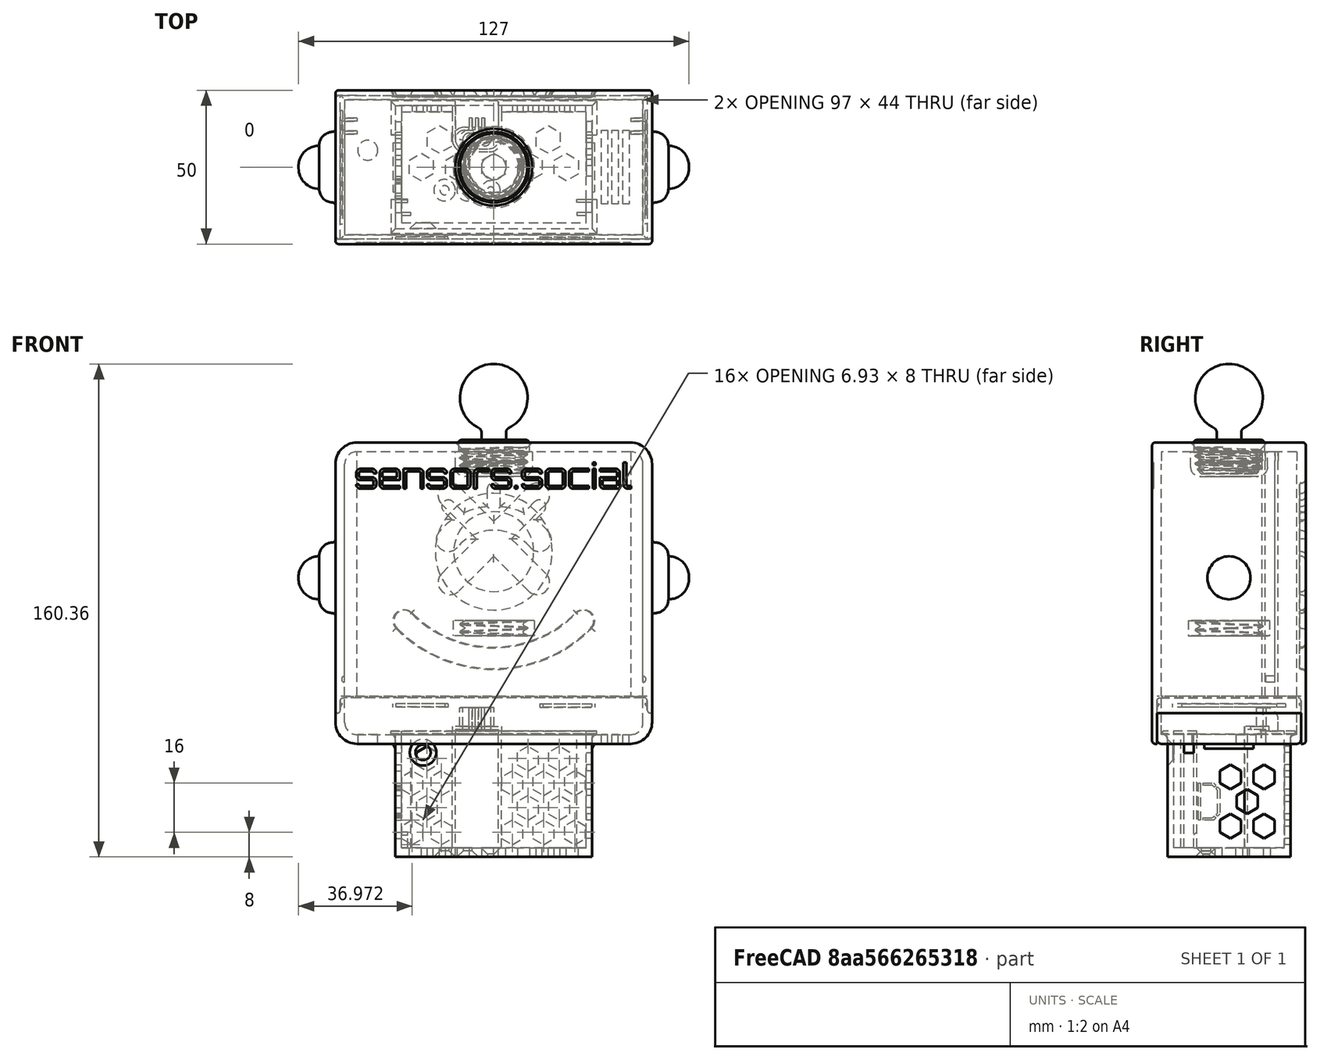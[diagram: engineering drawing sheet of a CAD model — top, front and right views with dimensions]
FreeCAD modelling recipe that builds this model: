
FCSTD DOCUMENT  (FreeCAD 1.1RUnknown)
Label: Altruist_Urban
License: All rights reserved
LicenseURL: http://en.wikipedia.org/wiki/All_rights_reserved
objects: Sketcher::SketchObject×33, PartDesign::Fillet×20, PartDesign::Pad×19, PartDesign::Pocket×16, App::Point×8, PartDesign::Body×8, PartDesign::Mirrored×5, PartDesign::Chamfer×5, PartDesign::FeatureBase×4, PartDesign::Thickness×2, PartDesign::Revolution×1, PartDesign::LinearPattern×1, PartDesign::Groove×1, Part::Part2DObjectPython×1, Part::FeaturePython×1, PartDesign::Boolean×1, PartDesign::Hole×1
note: 293 computed .brp shape members not serialized (recipe doc carries the construction recipe); baked Part::Feature solids carry a one-line shape summary decoded from their .brp

FEATURE [Sketcher::SketchObject] Sketch
  ArcFitTolerance = 1e-06
  AttachmentSupport = -> [XZ_Plane]
  ExternalTypes = [0]
  FullyConstrained = true
  MakeInternals = false
  MapMode = 5
  Placement = pos=(0,0,0) rot=(1,0,0;1.5708rad)
  _ExternalGeoVersion = 0
  sketch-geometry (4):
    g0: LineSegment StartX=-51.5 StartY=44 StartZ=0 EndX=-51.5 EndY=-44 EndZ=0
    g1: LineSegment StartX=-51.5 StartY=-44 StartZ=0 EndX=51.5 EndY=-44 EndZ=0
    g2: LineSegment StartX=51.5 StartY=-44 StartZ=0 EndX=51.5 EndY=44 EndZ=0
    g3: LineSegment StartX=51.5 StartY=44 StartZ=0 EndX=-51.5 EndY=44 EndZ=0
  constraints (11):
    c: Coincident(g0,g1)
    c: Coincident(g1,g2)
    c: Coincident(g2,g3)
    c: Coincident(g3,g0)
    c: Vertical(g0)
    c: Vertical(g2)
    c: Horizontal(g1)
    c: Horizontal(g3)
    c: DistanceX(g3,g3) = 103
    c: DistanceY(g2,g2) = 88
    c: Symmetric(g2,g0,g-1)
FEATURE [PartDesign::Pad] Pad
  Direction = (0,-1,2e-16)
  Length = 25
  Length2 = 25
  Placement = pos=(0,0,0) rot=(1,0,0;1.5708rad)
  Profile = -> Sketch
  ReferenceAxis = -> Sketch [N_Axis]
  Reversed = true
  SideType = 1
  Suppressed = false
  Type = 0
  Type2 = 0
FEATURE [PartDesign::Fillet] Fillet
  Base = -> Pad [Edge1,Edge8]
  BaseFeature = -> Pad
  Placement = pos=(0,0,0) rot=(1,0,0;1.5708rad)
  Radius = 7
  SupportTransform = false
  Suppressed = false
  UseAllEdges = false
FEATURE [Sketcher::SketchObject] Sketch009
  ArcFitTolerance = 1e-06
  AttachmentSupport = -> [XZ_Plane001]
  ExternalTypes = [0]
  FullyConstrained = true
  MakeInternals = false
  MapMode = 5
  Placement = pos=(0,0,0) rot=(1,0,0;1.5708rad)
  _ExternalGeoVersion = 0
  sketch-geometry (14):
    g0: ArcOfCircle CenterX=0 CenterY=6.86 CenterZ=0 NormalX=0 NormalY=0 NormalZ=1 AngleXU=0 Radius=11 StartAngle=5.16799 EndAngle=7.85398
    g1: LineSegment StartX=4 StartY=-6.86497 StartZ=0 EndX=10.5 EndY=-6.86497 EndZ=0
    g2: ArcOfCircle CenterX=10.5 CenterY=-7.86497 CenterZ=0 NormalX=0 NormalY=0 NormalZ=1 AngleXU=0 Radius=1 StartAngle=0 EndAngle=1.5708
    g3: LineSegment StartX=0 StartY=17.86 StartZ=0 EndX=0 EndY=-17.86 EndZ=0
    g4: LineSegment StartX=4 StartY=-6.86497 StartZ=0 EndX=4 EndY=-4.36497 EndZ=0
    g5: ArcOfCircle CenterX=5.5 CenterY=-4.36497 CenterZ=0 NormalX=0 NormalY=0 NormalZ=1 AngleXU=0 Radius=1.5 StartAngle=2.0264 EndAngle=3.14159
    g6: LineSegment [constr] StartX=0 StartY=6.86 StartZ=0 EndX=5.5 EndY=-4.36497 EndZ=0
    g7: LineSegment StartX=0 StartY=-17.86 StartZ=0 EndX=9 EndY=-17.86 EndZ=0
    g8: LineSegment StartX=9 StartY=-17.86 StartZ=0 EndX=10.7 EndY=-16.16 EndZ=0
    g9: LineSegment StartX=11.5 StartY=-7.86497 StartZ=0 EndX=11.5 EndY=-13.81 EndZ=0
    g10: LineSegment StartX=11.5 StartY=-13.81 StartZ=0 EndX=8.2 EndY=-13.81 EndZ=0
    g11: LineSegment StartX=8.2 StartY=-13.81 StartZ=0 EndX=8.2 EndY=-14.31 EndZ=0
    g12: LineSegment StartX=8.2 StartY=-14.31 StartZ=0 EndX=10.7 EndY=-14.31 EndZ=0
    g13: LineSegment StartX=10.7 StartY=-14.31 StartZ=0 EndX=10.7 EndY=-16.16 EndZ=0
  constraints (42):
    c: PointOnObject(g0,g-2)
    c: Radius(g0) = 11
    c: Horizontal(g1)
    c: Coincident(g2,g1)
    c: Coincident(g3,g0)
    c: Vertical(g1,g2)
    c: Horizontal(g2,g2)
    c: Radius(g2) = 1
    c: PointOnObject(g0,g3)
    c: Symmetric(g3,g0,g-1)
    c: Coincident(g4,g1)
    c: Vertical(g4)
    c: Coincident(g5,g0)
    c: Coincident(g5,g4)
    c: Horizontal(g4,g5)
    c: Coincident(g6,g0)
    c: Coincident(g6,g5)
    c: PointOnObject(g0,g6)
    c: Radius(g5) = 1.5
    c: DistanceY(g4,g4) = 2.5
    c: Distance(g3,g4) = 4
    c: DistanceY(g3,g3) = 35.72
    c: DistanceX(g1,g1) = 6.5
    c: Coincident(g3,g7)
    c: Horizontal(g7)
    c: Coincident(g7,g8)
    c: Angle(g8,g7) = 2.35619
    c: DistanceX(g7,g7) = 9
    c: Tangent(g2,g9) = 1.5708
    c: Coincident(g9,g10)
    c: Coincident(g10,g11)
    c: Vertical(g11)
    c: Coincident(g11,g12)
    c: Horizontal(g12)
    c: Coincident(g12,g13)
    c: Coincident(g13,g8)
    c: Vertical(g13)
    c: DistanceY(g11,g11) = 0.5
    c: Distance(g13,g3) = 10.7
    c: Distance(g12,g12) = 2.5
    c: DistanceY(g13,g13) = 1.85
    c: Horizontal(g10)
FEATURE [PartDesign::Revolution] Revolution
  Angle = 360
  Angle2 = 60
  Axis = (0,2e-16,1)
  Base = (0,0,0)
  FuseOrder = 1
  Placement = pos=(0,0,0) rot=(1,0,0;1.5708rad)
  Profile = -> Sketch009
  ReferenceAxis = -> Sketch009 [V_Axis]
  Reversed = true
  Suppressed = false
  Type = 0
FEATURE [Sketcher::SketchObject] Sketch010
  ArcFitTolerance = 1e-06
  AttachmentSupport = -> [XZ_Plane002]
  ExternalTypes = [0]
  FullyConstrained = true
  MakeInternals = false
  MapMode = 5
  Placement = pos=(0,0,0) rot=(1,0,0;1.5708rad)
  _ExternalGeoVersion = 0
  sketch-geometry (4):
    g0: LineSegment StartX=-51.5 StartY=7.5 StartZ=0 EndX=-51.5 EndY=-7.5 EndZ=0
    g1: LineSegment StartX=-51.5 StartY=-7.5 StartZ=0 EndX=51.5 EndY=-7.5 EndZ=0
    g2: LineSegment StartX=51.5 StartY=-7.5 StartZ=0 EndX=51.5 EndY=7.5 EndZ=0
    g3: LineSegment StartX=51.5 StartY=7.5 StartZ=0 EndX=-51.5 EndY=7.5 EndZ=0
  constraints (11):
    c: Coincident(g0,g1)
    c: Coincident(g1,g2)
    c: Coincident(g2,g3)
    c: Coincident(g3,g0)
    c: Vertical(g0)
    c: Vertical(g2)
    c: Horizontal(g1)
    c: Horizontal(g3)
    c: DistanceX(g3,g3) = 103
    c: Symmetric(g2,g0,g-1)
    c: DistanceY(g2,g2) = 15
FEATURE [PartDesign::Pad] Pad005
  Direction = (0,-1,2e-16)
  Length = 25
  Length2 = 25
  Placement = pos=(0,0,0) rot=(1,0,0;1.5708rad)
  Profile = -> Sketch010
  ReferenceAxis = -> Sketch010 [N_Axis]
  Reversed = true
  SideType = 1
  Suppressed = false
  Type = 0
  Type2 = 0
FEATURE [PartDesign::Fillet] Fillet004
  Base = -> Pad005 [Edge2,Edge5]
  BaseFeature = -> Pad005
  Placement = pos=(0,0,0) rot=(1,0,0;1.5708rad)
  Radius = 7
  SupportTransform = false
  Suppressed = false
  UseAllEdges = false
FEATURE [PartDesign::Thickness] Thickness001
  Base = -> Fillet004 [Face4]
  BaseFeature = -> Fillet004
  Intersection = false
  Join = 0
  Mode = 0
  Reversed = true
  SupportTransform = false
  Suppressed = false
  Value = 3
FEATURE [Sketcher::SketchObject] Sketch011
  ArcFitTolerance = 1e-06
  AttachmentSupport = -> [Thickness001]
  ExternalTypes = [0]
  FullyConstrained = true
  MakeInternals = false
  MapMode = 5
  Placement = pos=(0,-1e-15,-4.5) rot=(0,0,1;0rad)
  _ExternalGeoVersion = 0
  sketch-geometry (4):
    g0: LineSegment StartX=-32 StartY=20 StartZ=0 EndX=-32 EndY=-20 EndZ=0
    g1: LineSegment StartX=-32 StartY=-20 StartZ=0 EndX=32 EndY=-20 EndZ=0
    g2: LineSegment StartX=32 StartY=-20 StartZ=0 EndX=32 EndY=20 EndZ=0
    g3: LineSegment StartX=32 StartY=20 StartZ=0 EndX=-32 EndY=20 EndZ=0
  constraints (11):
    c: Coincident(g0,g1)
    c: Coincident(g1,g2)
    c: Coincident(g2,g3)
    c: Coincident(g3,g0)
    c: Vertical(g0)
    c: Vertical(g2)
    c: Horizontal(g1)
    c: Horizontal(g3)
    c: Symmetric(g2,g0,g-1)
    c: DistanceY(g2,g2) = 40
    c: DistanceX(g3,g3) = 64
FEATURE [PartDesign::Pocket] Pocket002
  BaseFeature = -> Thickness001
  Direction = (0,0,-1)
  Length = 5
  Length2 = 5
  Profile = -> Sketch011
  ReferenceAxis = -> Sketch011 [N_Axis]
  SideType = 0
  Suppressed = false
  Type = 1
  Type2 = 0
FEATURE [Sketcher::SketchObject] Sketch012
  ArcFitTolerance = 1e-06
  AttachmentSupport = -> [Pocket002]
  ExternalTypes = [0]
  FullyConstrained = true
  MakeInternals = false
  MapMode = 5
  Placement = pos=(0,1.7e-15,7.5) rot=(0,0,1;0rad)
  _ExternalGeoVersion = 0
  sketch-geometry (8):
    g0: LineSegment StartX=-49.9 StartY=23.4 StartZ=0 EndX=-49.9 EndY=-23.4 EndZ=0
    g1: LineSegment StartX=-49.9 StartY=-23.4 StartZ=0 EndX=49.9 EndY=-23.4 EndZ=0
    g2: LineSegment StartX=49.9 StartY=-23.4 StartZ=0 EndX=49.9 EndY=23.4 EndZ=0
    g3: LineSegment StartX=49.9 StartY=23.4 StartZ=0 EndX=-49.9 EndY=23.4 EndZ=0
    g4: LineSegment StartX=-51.5 StartY=25 StartZ=0 EndX=-51.5 EndY=-25 EndZ=0
    g5: LineSegment StartX=-51.5 StartY=-25 StartZ=0 EndX=51.5 EndY=-25 EndZ=0
    g6: LineSegment StartX=51.5 StartY=-25 StartZ=0 EndX=51.5 EndY=25 EndZ=0
    g7: LineSegment StartX=51.5 StartY=25 StartZ=0 EndX=-51.5 EndY=25 EndZ=0
  constraints (22):
    c: Coincident(g0,g1)
    c: Coincident(g1,g2)
    c: Coincident(g2,g3)
    c: Coincident(g3,g0)
    c: Vertical(g0)
    c: Vertical(g2)
    c: Horizontal(g1)
    c: Horizontal(g3)
    c: Symmetric(g0,g2,g-1)
    c: DistanceX(g3,g3) = 99.8
    c: DistanceY(g2,g2) = 46.8
    c: Coincident(g4,g5)
    c: Coincident(g5,g6)
    c: Coincident(g6,g7)
    c: Coincident(g7,g4)
    c: Vertical(g4)
    c: Vertical(g6)
    c: Horizontal(g5)
    c: Horizontal(g7)
    c: Symmetric(g4,g6,g-1)
    c: DistanceY(g6,g6) = 50
    c: DistanceX(g7,g7) = 103
FEATURE [PartDesign::Pocket] Pocket003
  BaseFeature = -> Pocket002
  Direction = (0,0,-1)
  Length = 5
  Length2 = 5
  Profile = -> Sketch012
  ReferenceAxis = -> Sketch012 [N_Axis]
  SideType = 0
  Suppressed = false
  Type = 0
  Type2 = 0
FEATURE [Sketcher::SketchObject] Sketch013
  ArcFitTolerance = 1e-06
  AttachmentSupport = -> [Pocket003]
  ExternalTypes = [0]
  FullyConstrained = true
  MakeInternals = false
  MapMode = 5
  Placement = pos=(0,-23.4,0) rot=(1,0,0;1.5708rad)
  _ExternalGeoVersion = 0
  sketch-geometry (6):
    g0: LineSegment StartX=49.9 StartY=5.55 StartZ=0 EndX=49.9 EndY=4.45 EndZ=0
    g1: LineSegment StartX=-49.15 StartY=5.55 StartZ=0 EndX=-49.9 EndY=5.55 EndZ=0
    g2: LineSegment StartX=-49.9 StartY=5.55 StartZ=0 EndX=-49.9 EndY=4.45 EndZ=0
    g3: LineSegment StartX=-49.9 StartY=4.45 StartZ=0 EndX=-49.15 EndY=5.55 EndZ=0
    g4: LineSegment StartX=49.9 StartY=5.55 StartZ=0 EndX=49.15 EndY=5.55 EndZ=0
    g5: LineSegment StartX=49.15 StartY=5.55 StartZ=0 EndX=49.9 EndY=4.45 EndZ=0
  constraints (17):
    c: Vertical(g0)
    c: Coincident(g1,g2)
    c: Vertical(g2)
    c: Equal(g0,g2)
    c: DistanceY(g0,g0) = 1.1
    c: Symmetric(g0,g2,g-2)
    c: DistanceX(g1,g0) = 99.8
    c: Coincident(g3,g2)
    c: Coincident(g3,g1)
    c: Coincident(g0,g4)
    c: Horizontal(g4)
    c: Coincident(g4,g5)
    c: Coincident(g5,g0)
    c: DistanceX(g4,g4) = 0.75
    c: Distance(g0,g-1) = 4.45
    c: Horizontal(g1)
    c: Equal(g1,g4)
FEATURE [PartDesign::Thickness] Thickness
  Base = -> Fillet [Face4]
  BaseFeature = -> Fillet
  Intersection = false
  Join = 0
  Mode = 0
  Reversed = true
  SupportTransform = false
  Suppressed = false
  Value = 3
FEATURE [Sketcher::SketchObject] Sketch004
  ArcFitTolerance = 1e-06
  AttachmentSupport = -> [Thickness]
  ExternalTypes = [0]
  FullyConstrained = true
  MakeInternals = false
  MapMode = 5
  Placement = pos=(0,-1.94e-14,-44) rot=(1,0,0;3.14159rad)
  _ExternalGeoVersion = 0
  sketch-geometry (4):
    g0: LineSegment StartX=-49.9 StartY=23.4 StartZ=0 EndX=-49.9 EndY=-23.4 EndZ=0
    g1: LineSegment StartX=-49.9 StartY=-23.4 StartZ=0 EndX=49.9 EndY=-23.4 EndZ=0
    g2: LineSegment StartX=49.9 StartY=-23.4 StartZ=0 EndX=49.9 EndY=23.4 EndZ=0
    g3: LineSegment StartX=49.9 StartY=23.4 StartZ=0 EndX=-49.9 EndY=23.4 EndZ=0
  constraints (11):
    c: Coincident(g0,g1)
    c: Coincident(g1,g2)
    c: Coincident(g2,g3)
    c: Coincident(g3,g0)
    c: Vertical(g0)
    c: Vertical(g2)
    c: Horizontal(g1)
    c: Horizontal(g3)
    c: Symmetric(g0,g2,g-1)
    c: DistanceX(g3,g3) = 99.8
    c: DistanceY(g2,g2) = 46.8
FEATURE [PartDesign::Pocket] Pocket001
  BaseFeature = -> Thickness
  Direction = (0,0,1)
  Length = 5.5
  Length2 = 5
  Profile = -> Sketch004
  ReferenceAxis = -> Sketch004 [N_Axis]
  SideType = 0
  Suppressed = false
  Type = 0
  Type2 = 0
FEATURE [Sketcher::SketchObject] Sketch005
  ArcFitTolerance = 1e-06
  AttachmentSupport = -> [Pocket001]
  ExternalGeometry = -> [Pocket001]
  ExternalTypes = [0]
  FullyConstrained = true
  MakeInternals = false
  MapMode = 5
  Placement = pos=(0,22,0) rot=(1,0,0;1.5708rad)
  _ExternalGeoVersion = 0
  sketch-geometry (8):
    g0: LineSegment StartX=-48.5 StartY=-38.5 StartZ=0 EndX=-48.5 EndY=37 EndZ=0
    g1: LineSegment StartX=-48.5 StartY=-38.5 StartZ=0 EndX=-44.5 EndY=-38.5 EndZ=0
    g2: LineSegment StartX=-44.5 StartY=-38.5 StartZ=0 EndX=-44.5 EndY=41 EndZ=0
    g3: LineSegment StartX=44.5 StartY=41 StartZ=0 EndX=44.5 EndY=-38.5 EndZ=0
    g4: LineSegment StartX=44.5 StartY=-38.5 StartZ=0 EndX=48.5 EndY=-38.5 EndZ=0
    g5: LineSegment StartX=48.5 StartY=-38.5 StartZ=0 EndX=48.5 EndY=37 EndZ=0
    g6: ArcOfCircle CenterX=44.5 CenterY=37 CenterZ=0 NormalX=0 NormalY=0 NormalZ=1 AngleXU=0 Radius=4 StartAngle=0 EndAngle=1.5708
    g7: ArcOfCircle CenterX=-44.5 CenterY=37 CenterZ=0 NormalX=0 NormalY=0 NormalZ=1 AngleXU=0 Radius=4 StartAngle=1.5708 EndAngle=3.14159
  constraints (22):
    c: Coincident(g0,g-4)
    c: Coincident(g1,g0)
    c: Horizontal(g1)
    c: Coincident(g2,g1)
    c: Vertical(g2)
    c: Vertical(g3)
    c: Coincident(g4,g3)
    c: Coincident(g5,g4)
    c: Coincident(g6,g3)
    c: Coincident(g7,g2)
    c: Coincident(g7,g0)
    c: PointOnObject(g7,g2)
    c: Coincident(g2,g-3)
    c: Coincident(g0,g-4)
    c: Coincident(g5,g6)
    c: Symmetric(g3,g1,g-2)
    c: Vertical(g5)
    c: Equal(g4,g1)
    c: PointOnObject(g6,g3)
    c: Horizontal(g6,g5)
    c: Horizontal(g4)
    c: Horizontal(g3,g2)
FEATURE [PartDesign::Pad] Pad004
  BaseFeature = -> Pocket001
  Direction = (0,-1,2e-16)
  Length = -6
  Length2 = 7
  Profile = -> Sketch005
  ReferenceAxis = -> Sketch005 [N_Axis]
  Reversed = true
  SideType = 1
  Suppressed = false
  Type = 0
  Type2 = 0
FEATURE [PartDesign::LinearPattern] LinearPattern
  BaseFeature = -> Pad004
  Direction = -> Y_Axis
  Length = 4.2
  Length2 = 100
  Mode = 0
  Mode2 = 0
  Occurrences = 2
  Occurrences2 = 1
  Offset = 4.2
  Offset2 = 10
  Originals = -> [Pad004]
  Reversed = true
  Reversed2 = false
  SpacingPattern = [0]
  SpacingPattern2 = [0]
  Spacings = [-1]
  Suppressed = false
  TransformMode = 0
FEATURE [Sketcher::SketchObject] Sketch006
  ArcFitTolerance = 1e-06
  AttachmentSupport = -> [LinearPattern]
  ExternalGeometry = -> [LinearPattern]
  ExternalTypes = [0]
  FullyConstrained = true
  MakeInternals = false
  MapMode = 5
  Placement = pos=(48.5,0,0) rot=(0.57735,-0.57735,-0.57735;2.0944rad)
  _ExternalGeoVersion = 0
  sketch-geometry (4):
    g0: LineSegment StartX=-12 StartY=-33 StartZ=0 EndX=-15 EndY=-33 EndZ=0
    g1: LineSegment StartX=-15 StartY=-33 StartZ=0 EndX=-15 EndY=-34 EndZ=0
    g2: LineSegment StartX=-15 StartY=-34 StartZ=0 EndX=-12 EndY=-34 EndZ=0
    g3: LineSegment StartX=-12 StartY=-34 StartZ=0 EndX=-12 EndY=-33 EndZ=0
  constraints (12):
    c: Coincident(g0,g1)
    c: Coincident(g1,g2)
    c: Coincident(g2,g3)
    c: Coincident(g3,g0)
    c: Horizontal(g0)
    c: Horizontal(g2)
    c: Vertical(g1)
    c: Vertical(g3)
    c: PointOnObject(g0,g-4)
    c: PointOnObject(g1,g-3)
    c: Distance(g-5,g2) = 5
    c: DistanceY(g3,g3) = 1
FEATURE [PartDesign::Groove] Groove
  Angle = 180
  Angle2 = 60
  Axis = (0,1,0)
  Base = (48.5,12,-33)
  BaseFeature = -> LinearPattern
  Profile = -> Sketch006
  ReferenceAxis = -> Sketch006 [Edge1]
  Reversed = true
  Suppressed = false
  Type = 0
FEATURE [PartDesign::Mirrored] Mirrored001
  BaseFeature = -> Groove
  MirrorPlane = -> YZ_Plane
  Originals = -> [Groove]
  Suppressed = false
  TransformMode = 0
FEATURE [Sketcher::SketchObject] Sketch007
  ArcFitTolerance = 1e-06
  AttachmentSupport = -> [Mirrored001]
  ExternalTypes = [0]
  FullyConstrained = true
  MakeInternals = false
  MapMode = 5
  Placement = pos=(-49.9,0,0) rot=(0.57735,0.57735,0.57735;2.0944rad)
  _ExternalGeoVersion = 0
  sketch-geometry (6):
    g0: LineSegment StartX=-23.4 StartY=-41 StartZ=0 EndX=-23.4 EndY=-42 EndZ=0
    g1: LineSegment StartX=23.4 StartY=-41 StartZ=0 EndX=23.4 EndY=-42 EndZ=0
    g2: LineSegment StartX=-23.4 StartY=-41 StartZ=0 EndX=-22.8 EndY=-41 EndZ=0
    g3: LineSegment StartX=-22.8 StartY=-41 StartZ=0 EndX=-23.4 EndY=-42 EndZ=0
    g4: LineSegment StartX=23.4 StartY=-41 StartZ=0 EndX=22.8 EndY=-41 EndZ=0
    g5: LineSegment StartX=22.8 StartY=-41 StartZ=0 EndX=23.4 EndY=-42 EndZ=0
  constraints (17):
    c: Vertical(g0)
    c: Vertical(g1)
    c: Equal(g0,g1)
    c: DistanceY(g1,g1) = 1
    c: Symmetric(g0,g1,g-2)
    c: Distance(g0,g1) = 46.8
    c: Coincident(g0,g2)
    c: Horizontal(g2)
    c: Coincident(g2,g3)
    c: Coincident(g3,g0)
    c: Coincident(g1,g4)
    c: Horizontal(g4)
    c: Coincident(g4,g5)
    c: Coincident(g5,g1)
    c: Equal(g4,g2)
    c: DistanceY(g1,g-1) = 41
    c: DistanceX(g4,g4) = 0.6
FEATURE [Sketcher::SketchObject] Sketch008
  ArcFitTolerance = 1e-06
  AttachmentSupport = -> [Pocket001]
  ExternalTypes = [0]
  FullyConstrained = true
  MakeInternals = false
  MapMode = 5
  Placement = pos=(0,23.4,0) rot=(1,0,0;1.5708rad)
  _ExternalGeoVersion = 0
  sketch-geometry (6):
    g0: LineSegment StartX=-49.9 StartY=-41 StartZ=0 EndX=-49.9 EndY=-42 EndZ=0
    g1: LineSegment StartX=49.9 StartY=-41 StartZ=0 EndX=49.9 EndY=-42 EndZ=0
    g2: LineSegment StartX=49.9 StartY=-41 StartZ=0 EndX=49.3 EndY=-41 EndZ=0
    g3: LineSegment StartX=49.3 StartY=-41 StartZ=0 EndX=49.9 EndY=-42 EndZ=0
    g4: LineSegment StartX=-49.9 StartY=-41 StartZ=0 EndX=-49.3 EndY=-41 EndZ=0
    g5: LineSegment StartX=-49.3 StartY=-41 StartZ=0 EndX=-49.9 EndY=-42 EndZ=0
  constraints (17):
    c: Vertical(g0)
    c: Vertical(g1)
    c: Equal(g0,g1)
    c: DistanceY(g1,g1) = 1
    c: Symmetric(g0,g1,g-2)
    c: Distance(g0,g1) = 99.8
    c: Coincident(g1,g2)
    c: Horizontal(g2)
    c: Coincident(g2,g3)
    c: Coincident(g3,g1)
    c: DistanceX(g2,g2) = 0.6
    c: Distance(g-1,g2) = 41
    c: Coincident(g0,g4)
    c: Horizontal(g4)
    c: Coincident(g4,g5)
    c: Coincident(g5,g0)
    c: Equal(g4,g2)
FEATURE [PartDesign::Fillet] Fillet023
  Base = -> Mirrored001 [Edge17,Edge15]
  BaseFeature = -> Mirrored001
  Radius = 1
  Refine = true
  SupportTransform = false
  Suppressed = false
  UseAllEdges = false
FEATURE [App::Point] Origin017  label="Origin"
  Role = Origin
FEATURE [App::Point] Origin018  label="Origin"
  Role = Origin
FEATURE [App::Point] Origin024  label="Origin"
  Role = Origin
FEATURE [App::Point] Origin025  label="Origin"
  Role = Origin
FEATURE [App::Point] Origin026  label="Origin"
  Role = Origin
FEATURE [App::Point] Origin029  label="Origin"
  Role = Origin
FEATURE [App::Point] Origin030  label="Origin"
  Role = Origin
FEATURE [App::Point] Origin032
  Role = Origin
FEATURE [Sketcher::SketchObject] Sketch099
  ArcFitTolerance = 1e-06
  AttachmentSupport = -> [XY_Plane017]
  ExternalTypes = [0]
  FullyConstrained = true
  MakeInternals = false
  MapMode = 5
  _ExternalGeoVersion = 0
  sketch-geometry (32):
    g0: LineSegment StartX=-32 StartY=-20 StartZ=0 EndX=32 EndY=-20 EndZ=0
    g1: LineSegment StartX=-32 StartY=20 StartZ=0 EndX=-32 EndY=-20 EndZ=0
    g2: LineSegment StartX=32 StartY=20 StartZ=0 EndX=32 EndY=-20 EndZ=0
    g3: LineSegment StartX=-30 StartY=-18 StartZ=0 EndX=30 EndY=-18 EndZ=0
    g4: LineSegment StartX=-30 StartY=18 StartZ=0 EndX=-13.5 EndY=18 EndZ=0
    g5: LineSegment StartX=30 StartY=18 StartZ=0 EndX=2.5 EndY=18 EndZ=0
    g6: LineSegment StartX=-9.5 StartY=5 StartZ=0 EndX=-1.5 EndY=5 EndZ=0
    g7: LineSegment StartX=-32 StartY=20 StartZ=0 EndX=-12.5 EndY=20 EndZ=0
    g8: LineSegment StartX=32 StartY=20 StartZ=0 EndX=1.5 EndY=20 EndZ=0
    g9: LineSegment StartX=-9.5 StartY=6 StartZ=0 EndX=-1.5 EndY=6 EndZ=0
    g10: LineSegment StartX=-12.5 StartY=20 StartZ=0 EndX=-12.5 EndY=9 EndZ=0
    g11: LineSegment StartX=1.5 StartY=20 StartZ=0 EndX=1.5 EndY=9 EndZ=0
    g12: ArcOfCircle CenterX=-9.5 CenterY=9 CenterZ=0 NormalX=0 NormalY=0 NormalZ=1 AngleXU=0 Radius=3 StartAngle=3.14159 EndAngle=4.71239
    g13: ArcOfCircle CenterX=-1.5 CenterY=9 CenterZ=0 NormalX=0 NormalY=0 NormalZ=1 AngleXU=0 Radius=3 StartAngle=4.71239 EndAngle=6.28319
    g14: LineSegment StartX=-13.5 StartY=18 StartZ=0 EndX=-13.5 EndY=9 EndZ=0
    g15: LineSegment StartX=2.5 StartY=18 StartZ=0 EndX=2.5 EndY=9 EndZ=0
    g16: ArcOfCircle CenterX=-9.5 CenterY=9 CenterZ=0 NormalX=0 NormalY=0 NormalZ=1 AngleXU=0 Radius=4 StartAngle=3.14159 EndAngle=4.71239
    g17: ArcOfCircle CenterX=-1.5 CenterY=9 CenterZ=0 NormalX=0 NormalY=0 NormalZ=1 AngleXU=0 Radius=4 StartAngle=4.71239 EndAngle=6.28319
    g18: LineSegment StartX=-30 StartY=-15.7 StartZ=0 EndX=-27 EndY=-15.7 EndZ=0
    g19: LineSegment StartX=-27 StartY=-15.7 StartZ=0 EndX=-27 EndY=-14.7 EndZ=0
    g20: LineSegment StartX=-27 StartY=-14.7 StartZ=0 EndX=-30 EndY=-14.7 EndZ=0
    g21: LineSegment StartX=30 StartY=-14.7 StartZ=0 EndX=27 EndY=-14.7 EndZ=0
    g22: LineSegment StartX=27 StartY=-14.7 StartZ=0 EndX=27 EndY=-15.7 EndZ=0
    g23: LineSegment StartX=27 StartY=-15.7 StartZ=0 EndX=30 EndY=-15.7 EndZ=0
    g24: LineSegment StartX=-30 StartY=18 StartZ=0 EndX=-30 EndY=-14.7 EndZ=0
    g25: LineSegment StartX=-30 StartY=-15.7 StartZ=0 EndX=-30 EndY=-18 EndZ=0
    g26: LineSegment StartX=30 StartY=-18 StartZ=0 EndX=30 EndY=-15.7 EndZ=0
    g27: LineSegment StartX=30 StartY=-14.7 StartZ=0 EndX=30 EndY=-11.5 EndZ=0
    g28: LineSegment StartX=30 StartY=-11.5 StartZ=0 EndX=27 EndY=-11.5 EndZ=0
    g29: LineSegment StartX=27 StartY=-11.5 StartZ=0 EndX=27 EndY=-10.5 EndZ=0
    g30: LineSegment StartX=27 StartY=-10.5 StartZ=0 EndX=30 EndY=-10.5 EndZ=0
    g31: LineSegment StartX=30 StartY=-10.5 StartZ=0 EndX=30 EndY=18 EndZ=0
  constraints (95):
    c: Horizontal(g0)
    c: Symmetric(g2,g0,g-1)
    c: DistanceY(g0,g2) = 40
    c: DistanceX(g1,g2) = 64
    c: Vertical(g1)
    c: Vertical(g2)
    c: Coincident(g0,g1)
    c: Coincident(g2,g0)
    c: Horizontal(g3)
    c: Symmetric(g3,g5,g-1)
    c: DistanceX(g4,g5) = 60
    c: Horizontal(g4)
    c: Horizontal(g5)
    c: DistanceY(g3,g5) = 36
    c: Horizontal(g6)
    c: Coincident(g7,g1)
    c: Horizontal(g7)
    c: Coincident(g8,g2)
    c: Horizontal(g8)
    c: Horizontal(g9)
    c: Coincident(g10,g7)
    c: Vertical(g10)
    c: Coincident(g11,g8)
    c: Vertical(g11)
    c: Coincident(g12,g10)
    c: Coincident(g12,g9)
    c: Coincident(g13,g9)
    c: Coincident(g13,g11)
    c: Equal(g1,g2)
    c: Coincident(g14,g4)
    c: Vertical(g14)
    c: Coincident(g15,g5)
    c: Vertical(g15)
    c: Horizontal(g10,g12)
    c: Horizontal(g13,g11)
    c: Equal(g13,g12)
    c: Coincident(g16,g12)
    c: Coincident(g16,g14)
    c: Coincident(g16,g6)
    c: Coincident(g17,g13)
    c: Coincident(g17,g15)
    c: Coincident(g17,g6)
    c: Horizontal(g15,g13)
    c: Horizontal(g14,g12)
    c: Vertical(g12,g9)
    c: Vertical(g12,g6)
    c: Vertical(g13,g9)
    c: Vertical(g13,g6)
    c: Distance(g10,g14) = 1
    c: DistanceX(g7,g8) = 14
    c: Distance(g9,g4) = 12
    c: Radius(g13) = 3
    c: DistanceX(g7,g7) = 19.5
    c: Coincident(g18,g19)
    c: Coincident(g19,g20)
    c: Vertical(g19)
    c: Horizontal(g18)
    c: Horizontal(g20)
    c: Coincident(g21,g22)
    c: Coincident(g22,g23)
    c: Horizontal(g21)
    c: Horizontal(g23)
    c: Vertical(g22)
    c: DistanceX(g24,g27) = 60
    c: Horizontal(g21,g19)
    c: Coincident(g24,g4)
    c: Coincident(g25,g18)
    c: Coincident(g25,g3)
    c: Vertical(g25)
    c: Symmetric(g3,g4,g-1)
    c: Coincident(g26,g3)
    c: Coincident(g26,g23)
    c: Vertical(g26)
    c: Coincident(g31,g5)
    c: Equal(g21,g23)
    c: Distance(g3,g18) = 2.3
    c: Distance(g19,g19) = 1
    c: DistanceX(g18,g18) = 3
    c: Coincident(g24,g20)
    c: Equal(g18,g20)
    c: Horizontal(g18,g22)
    c: Equal(g23,g18)
    c: Coincident(g21,g27)
    c: Horizontal(g28)
    c: Coincident(g28,g29)
    c: Vertical(g29)
    c: Coincident(g29,g30)
    c: Horizontal(g30)
    c: Coincident(g28,g27)
    c: Coincident(g30,g31)
    c: Equal(g29,g22)
    c: Equal(g28,g21)
    c: Vertical(g27)
    c: DistanceY(g27,g27) = 3.2
    c: Vertical(g31)
FEATURE [PartDesign::Pad] Pad084
  Direction = (0,0,1)
  Length = 40
  Length2 = 10
  Profile = -> Sketch099
  ReferenceAxis = -> Sketch099 [N_Axis]
  SideType = 0
  Suppressed = false
  Type = 0
  Type2 = 0
FEATURE [Sketcher::SketchObject] Sketch100
  ArcFitTolerance = 1e-06
  AttachmentSupport = -> [Pad084]
  ExternalTypes = [0]
  FullyConstrained = true
  MakeInternals = false
  MapMode = 5
  Placement = pos=(0,0,40) rot=(0,0,1;0rad)
  _ExternalGeoVersion = 0
  sketch-geometry (22):
    g0: LineSegment StartX=-33.5 StartY=-21.5 StartZ=0 EndX=33.5 EndY=-21.5 EndZ=0
    g1: LineSegment StartX=-33.5 StartY=21.5 StartZ=0 EndX=-33.5 EndY=10.5 EndZ=0
    g2: LineSegment StartX=33.5 StartY=21.5 StartZ=0 EndX=33.5 EndY=10.5 EndZ=0
    g3: LineSegment StartX=-30 StartY=18 StartZ=0 EndX=-30 EndY=10.5 EndZ=0
    g4: LineSegment StartX=-30 StartY=-18 StartZ=0 EndX=30 EndY=-18 EndZ=0
    g5: LineSegment StartX=30 StartY=-18 StartZ=0 EndX=30 EndY=-10.5 EndZ=0
    g6: LineSegment StartX=-30 StartY=18 StartZ=0 EndX=-13.5 EndY=18 EndZ=0
    g7: LineSegment StartX=30 StartY=18 StartZ=0 EndX=2.5 EndY=18 EndZ=0
    g8: LineSegment StartX=33.5 StartY=21.5 StartZ=0 EndX=-33.5 EndY=21.5 EndZ=0
    g9: LineSegment StartX=-13.5 StartY=18 StartZ=0 EndX=-13.5 EndY=9 EndZ=0
    g10: LineSegment StartX=2.5 StartY=18 StartZ=0 EndX=2.5 EndY=9 EndZ=0
    g11: LineSegment StartX=30 StartY=-10.5 StartZ=0 EndX=33.5 EndY=-10.5 EndZ=0
    g12: LineSegment StartX=-33.5 StartY=-10.5 StartZ=0 EndX=-30 EndY=-10.5 EndZ=0
    g13: LineSegment StartX=-33.5 StartY=10.5 StartZ=0 EndX=-30 EndY=10.5 EndZ=0
    g14: LineSegment StartX=30 StartY=10.5 StartZ=0 EndX=33.5 EndY=10.5 EndZ=0
    g15: LineSegment StartX=33.5 StartY=-10.5 StartZ=0 EndX=33.5 EndY=-21.5 EndZ=0
    g16: LineSegment StartX=30 StartY=10.5 StartZ=0 EndX=30 EndY=18 EndZ=0
    g17: LineSegment StartX=-33.5 StartY=-10.5 StartZ=0 EndX=-33.5 EndY=-21.5 EndZ=0
    g18: LineSegment StartX=-30 StartY=-10.5 StartZ=0 EndX=-30 EndY=-18 EndZ=0
    g19: ArcOfCircle CenterX=-9.5 CenterY=9 CenterZ=0 NormalX=0 NormalY=0 NormalZ=1 AngleXU=0 Radius=4 StartAngle=1.5708 EndAngle=3.14159
    g20: ArcOfCircle CenterX=-1.5 CenterY=9 CenterZ=0 NormalX=0 NormalY=0 NormalZ=1 AngleXU=0 Radius=4 StartAngle=1e-16 EndAngle=1.5708
    g21: LineSegment StartX=-9.5 StartY=13 StartZ=0 EndX=-1.5 EndY=13 EndZ=0
  constraints (65):
    c: Horizontal(g0)
    c: Symmetric(g2,g0,g-1)
    c: DistanceY(g0,g2) = 43
    c: DistanceX(g1,g2) = 67
    c: Coincident(g0,g17)
    c: Coincident(g15,g0)
    c: Coincident(g18,g4)
    c: Coincident(g4,g5)
    c: Horizontal(g4)
    c: Symmetric(g18,g16,g-1)
    c: DistanceX(g3,g16) = 60
    c: Coincident(g6,g3)
    c: Horizontal(g6)
    c: Coincident(g7,g16)
    c: Horizontal(g7)
    c: DistanceY(g5,g16) = 36
    c: Coincident(g8,g2)
    c: Horizontal(g8)
    c: Coincident(g9,g6)
    c: Vertical(g9)
    c: Coincident(g10,g7)
    c: Vertical(g10)
    c: Horizontal(g9,g19)
    c: Distance(g10,g9) = 16
    c: Coincident(g1,g8)
    c: DistanceX(g6,g6) = 16.5
    c: Horizontal(g11)
    c: Horizontal(g12)
    c: Horizontal(g11,g12)
    c: Horizontal(g13)
    c: Horizontal(g14)
    c: Horizontal(g14,g13)
    c: Symmetric(g14,g11,g-1)
    c: Vertical(g2)
    c: Vertical(g15)
    c: Coincident(g11,g15)
    c: Coincident(g2,g14)
    c: Vertical(g5)
    c: Vertical(g16)
    c: Coincident(g11,g5)
    c: Coincident(g14,g16)
    c: Vertical(g1)
    c: Vertical(g17)
    c: Coincident(g12,g17)
    c: Coincident(g13,g1)
    c: Vertical(g3)
    c: Vertical(g18)
    c: Coincident(g12,g18)
    c: Coincident(g13,g3)
    c: Vertical(g1,g12)
    c: Distance(g11,g14) = 21
    c: Equal(g13,g14)
    c: Equal(g14,g11)
    c: Horizontal(g6,g7)
    c: DistanceY(g9,g9) = 9
    c: Angle(g19) = 1.5708
    c: Coincident(g19,g9)
    c: Radius(g19) = 4
    c: Coincident(g20,g10)
    c: Equal(g20,g19)
    c: Horizontal(g20,g10)
    c: Coincident(g21,g19)
    c: Coincident(g21,g20)
    c: Horizontal(g21)
    c: Vertical(g20,g20)
FEATURE [PartDesign::Pad] Pad086
  BaseFeature = -> Pad084
  Direction = (0,0,1)
  Length = 1
  Length2 = 10
  Profile = -> Sketch100
  ReferenceAxis = -> Sketch100 [N_Axis]
  SideType = 0
  Suppressed = false
  Type = 0
  Type2 = 0
FEATURE [PartDesign::Pad] Pad085
  BaseFeature = -> Pad086
  Direction = (0,0,1)
  Length = 3
  Length2 = 10
  Profile = -> Sketch099 [Edge4,Edge5,Edge6,Edge7,Edge8,Edge9,Edge10,Edge1,Edge2,Edge3]
  ReferenceAxis = -> Sketch099 [N_Axis]
  SideType = 0
  Suppressed = false
  Type = 0
  Type2 = 0
FEATURE [Sketcher::SketchObject] Sketch101
  ArcFitTolerance = 1e-06
  AttachmentSupport = -> [Pad084]
  ExternalTypes = [0]
  FullyConstrained = true
  MakeInternals = false
  MapMode = 5
  Placement = pos=(-32,0,0) rot=(0.57735,-0.57735,-0.57735;2.0944rad)
  _ExternalGeoVersion = 0
  sketch-geometry (39):
    g0: LineSegment StartX=-7.9282 StartY=24 StartZ=0 EndX=-7.9282 EndY=28 EndZ=0
    g1: LineSegment StartX=-7.9282 StartY=28 StartZ=0 EndX=-11.3923 EndY=30 EndZ=0
    g2: LineSegment StartX=-11.3923 StartY=30 StartZ=0 EndX=-14.8564 EndY=28 EndZ=0
    g3: LineSegment StartX=-14.8564 StartY=28 StartZ=0 EndX=-14.8564 EndY=24 EndZ=0
    g4: LineSegment StartX=-14.8564 StartY=24 StartZ=0 EndX=-11.3923 EndY=22 EndZ=0
    g5: LineSegment StartX=-11.3923 StartY=22 StartZ=0 EndX=-7.9282 EndY=24 EndZ=0
    g6: Circle [constr] CenterX=-11.3923 CenterY=26 CenterZ=0 NormalX=0 NormalY=0 NormalZ=1 AngleXU=0 Radius=4
    g7: LineSegment StartX=3 StartY=24 StartZ=0 EndX=3 EndY=28 EndZ=0
    g8: LineSegment StartX=3 StartY=28 StartZ=0 EndX=-0.464102 EndY=30 EndZ=0
    g9: LineSegment StartX=-0.464102 StartY=30 StartZ=0 EndX=-3.9282 EndY=28 EndZ=0
    g10: LineSegment StartX=-3.9282 StartY=28 StartZ=0 EndX=-3.9282 EndY=24 EndZ=0
    g11: LineSegment StartX=-3.9282 StartY=24 StartZ=0 EndX=-0.464102 EndY=22 EndZ=0
    g12: LineSegment StartX=-0.464102 StartY=22 StartZ=0 EndX=3 EndY=24 EndZ=0
    g13: Circle [constr] CenterX=-0.464102 CenterY=26 CenterZ=0 NormalX=0 NormalY=0 NormalZ=1 AngleXU=0 Radius=4
    g14: LineSegment StartX=-2.4641 StartY=16 StartZ=0 EndX=-2.4641 EndY=20 EndZ=0
    g15: LineSegment StartX=-2.4641 StartY=20 StartZ=0 EndX=-5.9282 EndY=22 EndZ=0
    g16: LineSegment StartX=-5.9282 StartY=22 StartZ=0 EndX=-9.3923 EndY=20 EndZ=0
    g17: LineSegment StartX=-9.3923 StartY=20 StartZ=0 EndX=-9.3923 EndY=16 EndZ=0
    g18: LineSegment StartX=-9.3923 StartY=16 StartZ=0 EndX=-5.9282 EndY=14 EndZ=0
    g19: LineSegment StartX=-5.9282 StartY=14 StartZ=0 EndX=-2.4641 EndY=16 EndZ=0
    g20: Circle [constr] CenterX=-5.9282 CenterY=18 CenterZ=0 NormalX=0 NormalY=0 NormalZ=1 AngleXU=0 Radius=4
    g21: LineSegment StartX=-7.9282 StartY=8 StartZ=0 EndX=-7.9282 EndY=12 EndZ=0
    g22: LineSegment StartX=-7.9282 StartY=12 StartZ=0 EndX=-11.3923 EndY=14 EndZ=0
    g23: LineSegment StartX=-11.3923 StartY=14 StartZ=0 EndX=-14.8564 EndY=12 EndZ=0
    g24: LineSegment StartX=-14.8564 StartY=12 StartZ=0 EndX=-14.8564 EndY=8 EndZ=0
    g25: LineSegment StartX=-14.8564 StartY=8 StartZ=0 EndX=-11.3923 EndY=6 EndZ=0
    g26: LineSegment StartX=-11.3923 StartY=6 StartZ=0 EndX=-7.9282 EndY=8 EndZ=0
    g27: Circle [constr] CenterX=-11.3923 CenterY=10 CenterZ=0 NormalX=0 NormalY=0 NormalZ=1 AngleXU=0 Radius=4
    g28: LineSegment StartX=3 StartY=8 StartZ=0 EndX=3 EndY=12 EndZ=0
    g29: LineSegment StartX=3 StartY=12 StartZ=0 EndX=-0.464102 EndY=14 EndZ=0
    g30: LineSegment StartX=-0.464102 StartY=14 StartZ=0 EndX=-3.9282 EndY=12 EndZ=0
    g31: LineSegment StartX=-3.9282 StartY=12 StartZ=0 EndX=-3.9282 EndY=8 EndZ=0
    g32: LineSegment StartX=-3.9282 StartY=8 StartZ=0 EndX=-0.464102 EndY=6 EndZ=0
    g33: LineSegment StartX=-0.464102 StartY=6 StartZ=0 EndX=3 EndY=8 EndZ=0
    g34: Circle [constr] CenterX=-0.464102 CenterY=10 CenterZ=0 NormalX=0 NormalY=0 NormalZ=1 AngleXU=0 Radius=4
    g35: LineSegment StartX=11.5 StartY=37 StartZ=0 EndX=11.5 EndY=33.8 EndZ=0
    g36: LineSegment StartX=11.5 StartY=33.8 StartZ=0 EndX=14.7 EndY=33.8 EndZ=0
    g37: LineSegment StartX=14.7 StartY=33.8 StartZ=0 EndX=14.7 EndY=37 EndZ=0
    g38: LineSegment StartX=14.7 StartY=37 StartZ=0 EndX=11.5 EndY=37 EndZ=0
  constraints (95):
    c: Coincident(g0,g1)
    c: Coincident(g1,g2)
    c: Coincident(g2,g3)
    c: Coincident(g3,g4)
    c: Coincident(g4,g5)
    c: Coincident(g5,g0)
    c: Equal(g0, g1-g5) x5
    c: PointOnObject(g0,g6)
    c: PointOnObject(g1,g6)
    c: PointOnObject(g2,g6)
    c: PointOnObject(g3,g6)
    c: PointOnObject(g4,g6)
    c: PointOnObject(g5,g6)
    c: Vertical(g0)
    c: Coincident(g7,g8)
    c: Coincident(g8,g9)
    c: Coincident(g9,g10)
    c: Coincident(g10,g11)
    c: Coincident(g11,g12)
    c: Coincident(g12,g7)
    c: Equal(g7, g8-g12) x5
    c: PointOnObject(g7,g13)
    c: PointOnObject(g8,g13)
    c: PointOnObject(g9,g13)
    c: PointOnObject(g10,g13)
    c: PointOnObject(g11,g13)
    c: PointOnObject(g12,g13)
    c: Vertical(g7)
    c: Equal(g3,g10)
    c: DistanceY(g3,g3) = 4
    c: Coincident(g14,g15)
    c: Coincident(g15,g16)
    c: Coincident(g16,g17)
    c: Coincident(g17,g18)
    c: Coincident(g18,g19)
    c: Coincident(g19,g14)
    c: Equal(g14, g15-g19) x5
    c: PointOnObject(g14,g20)
    c: PointOnObject(g15,g20)
    c: PointOnObject(g16,g20)
    c: PointOnObject(g17,g20)
    c: PointOnObject(g18,g20)
    c: PointOnObject(g19,g20)
    c: Vertical(g14)
    c: Equal(g3,g17)
    c: Coincident(g21,g22)
    c: Coincident(g22,g23)
    c: Coincident(g23,g24)
    c: Coincident(g24,g25)
    c: Coincident(g25,g26)
    c: Coincident(g26,g21)
    c: Equal(g21, g22-g26) x5
    c: PointOnObject(g21,g27)
    c: PointOnObject(g22,g27)
    c: PointOnObject(g23,g27)
    c: PointOnObject(g24,g27)
    c: PointOnObject(g25,g27)
    c: PointOnObject(g26,g27)
    c: Vertical(g21)
    c: Equal(g24,g3)
    c: Vertical(g27,g6)
    c: Coincident(g28,g29)
    c: Coincident(g29,g30)
    c: Coincident(g30,g31)
    c: Coincident(g31,g32)
    c: Coincident(g32,g33)
    c: Coincident(g33,g28)
    c: Equal(g28, g29-g33) x5
    c: PointOnObject(g28,g34)
    c: PointOnObject(g29,g34)
    c: PointOnObject(g30,g34)
    c: PointOnObject(g31,g34)
    c: PointOnObject(g32,g34)
    c: PointOnObject(g33,g34)
    c: Equal(g31,g3)
    c: Symmetric(g22,g29,g18)
    c: Symmetric(g4,g11,g15)
    c: Distance(g10,g0) = 4
    c: Distance(g27,g-1) = 10
    c: Coincident(g35,g36)
    c: Coincident(g36,g37)
    c: Coincident(g37,g38)
    c: Coincident(g38,g35)
    c: Vertical(g35)
    c: Vertical(g37)
    c: Horizontal(g36)
    c: Horizontal(g38)
    c: DistanceX(g38,g38) = 3.2
    c: Equal(g37,g38)
    c: Distance(g35,g-2) = 11.5
    c: Distance(g-1,g38) = 37
    c: Vertical(g31)
    c: Horizontal(g21,g30)
    c: Horizontal(g0,g10)
    c: Distance(g-2,g7) = 3
FEATURE [PartDesign::Pocket] Pocket039
  BaseFeature = -> Pad085
  Direction = (1,0,0)
  Length = 5
  Length2 = 5
  Profile = -> Sketch101
  ReferenceAxis = -> Sketch101 [N_Axis]
  SideType = 0
  Suppressed = false
  Type = 2
  Type2 = 0
FEATURE [PartDesign::Mirrored] Mirrored010
  BaseFeature = -> Pocket039
  MirrorPlane = -> YZ_Plane017
  Originals = -> [Pocket039]
  Suppressed = false
  TransformMode = 0
FEATURE [Sketcher::SketchObject] Sketch102
  ArcFitTolerance = 1e-06
  ExternalTypes = [0]
  FullyConstrained = true
  MakeInternals = false
  MapMode = 5
  Placement = pos=(0,-20,0) rot=(1,0,0;1.5708rad)
  _ExternalGeoVersion = 0
  sketch-geometry (1):
    g0: Circle CenterX=-23 CenterY=34 CenterZ=0 NormalX=0 NormalY=0 NormalZ=1 AngleXU=0 Radius=2.5
  constraints (3):
    c: Distance(g0,g-2) = 23
    c: DistanceY(g-1,g0) = 34
    c: Diameter(g0) = 5
FEATURE [PartDesign::Pocket] Pocket040
  BaseFeature = -> Mirrored010
  Direction = (0,1,-2e-16)
  Length = 5
  Length2 = 5
  Profile = -> Sketch102
  ReferenceAxis = -> Sketch102 [N_Axis]
  SideType = 0
  Suppressed = false
  Type = 2
  Type2 = 0
FEATURE [Sketcher::SketchObject] Sketch103
  ArcFitTolerance = 1e-06
  AttachmentSupport = -> [Pocket040]
  ExternalTypes = [0]
  FullyConstrained = true
  MakeInternals = false
  MapMode = 5
  Placement = pos=(0,0,0) rot=(1,0,0;3.14159rad)
  _ExternalGeoVersion = 0
  sketch-geometry (52):
    g0: Circle CenterX=-8.5 CenterY=7.5 CenterZ=0 NormalX=0 NormalY=0 NormalZ=1 AngleXU=0 Radius=1.5
    g1: Circle CenterX=-16 CenterY=7.5 CenterZ=0 NormalX=0 NormalY=0 NormalZ=1 AngleXU=0 Radius=1.5
    g2: Circle CenterX=-1 CenterY=7.5 CenterZ=0 NormalX=0 NormalY=0 NormalZ=1 AngleXU=0 Radius=1.1
    g3: LineSegment StartX=3.89711 StartY=-2.25 StartZ=0 EndX=3.89711 EndY=2.25 EndZ=0
    g4: LineSegment StartX=3.89711 StartY=2.25 StartZ=0 EndX=0 EndY=4.5 EndZ=0
    g5: LineSegment StartX=0 StartY=4.5 StartZ=0 EndX=-3.89711 EndY=2.25 EndZ=0
    g6: LineSegment StartX=-3.89711 StartY=2.25 StartZ=0 EndX=-3.89711 EndY=-2.25 EndZ=0
    g7: LineSegment StartX=-3.89711 StartY=-2.25 StartZ=0 EndX=4e-16 EndY=-4.5 EndZ=0
    g8: LineSegment StartX=4e-16 StartY=-4.5 StartZ=0 EndX=3.89711 EndY=-2.25 EndZ=0
    g9: Circle [constr] CenterX=0 CenterY=0 CenterZ=0 NormalX=0 NormalY=0 NormalZ=1 AngleXU=0 Radius=4.5
    g10: LineSegment StartX=27.4856 StartY=-2.25 StartZ=0 EndX=27.4856 EndY=2.25 EndZ=0
    g11: LineSegment StartX=27.4856 StartY=2.25 StartZ=0 EndX=23.5885 EndY=4.5 EndZ=0
    g12: LineSegment StartX=23.5885 StartY=4.5 StartZ=0 EndX=19.6913 EndY=2.25 EndZ=0
    g13: LineSegment StartX=19.6913 StartY=2.25 StartZ=0 EndX=19.6913 EndY=-2.25 EndZ=0
    g14: LineSegment StartX=19.6913 StartY=-2.25 StartZ=0 EndX=23.5885 EndY=-4.5 EndZ=0
    g15: LineSegment StartX=23.5885 StartY=-4.5 StartZ=0 EndX=27.4856 EndY=-2.25 EndZ=0
    g16: Circle [constr] CenterX=23.5885 CenterY=0 CenterZ=0 NormalX=0 NormalY=0 NormalZ=1 AngleXU=0 Radius=4.5
    g17: LineSegment StartX=-7.89711 StartY=-2.25 StartZ=0 EndX=-7.89711 EndY=2.25 EndZ=0
    g18: LineSegment StartX=-7.89711 StartY=2.25 StartZ=0 EndX=-11.7942 EndY=4.5 EndZ=0
    g19: LineSegment StartX=-11.7942 StartY=4.5 StartZ=0 EndX=-15.6913 EndY=2.25 EndZ=0
    g20: LineSegment StartX=-15.6913 StartY=2.25 StartZ=0 EndX=-15.6913 EndY=-2.25 EndZ=0
    g21: LineSegment StartX=-15.6913 StartY=-2.25 StartZ=0 EndX=-11.7942 EndY=-4.5 EndZ=0
    g22: LineSegment StartX=-11.7942 StartY=-4.5 StartZ=0 EndX=-7.89711 EndY=-2.25 EndZ=0
    g23: Circle [constr] CenterX=-11.7942 CenterY=0 CenterZ=0 NormalX=0 NormalY=0 NormalZ=1 AngleXU=0 Radius=4.5
    g24: LineSegment StartX=-19.6913 StartY=-2.25 StartZ=0 EndX=-19.6913 EndY=2.25 EndZ=0
    g25: LineSegment StartX=-19.6913 StartY=2.25 StartZ=0 EndX=-23.5885 EndY=4.5 EndZ=0
    g26: LineSegment StartX=-23.5885 StartY=4.5 StartZ=0 EndX=-27.4856 EndY=2.25 EndZ=0
    g27: LineSegment StartX=-27.4856 StartY=2.25 StartZ=0 EndX=-27.4856 EndY=-2.25 EndZ=0
    g28: LineSegment StartX=-27.4856 StartY=-2.25 StartZ=0 EndX=-23.5885 EndY=-4.5 EndZ=0
    g29: LineSegment StartX=-23.5885 StartY=-4.5 StartZ=0 EndX=-19.6913 EndY=-2.25 EndZ=0
    g30: Circle [constr] CenterX=-23.5885 CenterY=0 CenterZ=0 NormalX=0 NormalY=0 NormalZ=1 AngleXU=0 Radius=4.5
    g31: LineSegment StartX=15.6913 StartY=-2.25 StartZ=0 EndX=15.6913 EndY=2.25 EndZ=0
    g32: LineSegment StartX=15.6913 StartY=2.25 StartZ=0 EndX=11.7942 EndY=4.5 EndZ=0
    g33: LineSegment StartX=11.7942 StartY=4.5 StartZ=0 EndX=7.89711 EndY=2.25 EndZ=0
    g34: LineSegment StartX=7.89711 StartY=2.25 StartZ=0 EndX=7.89711 EndY=-2.25 EndZ=0
    g35: LineSegment StartX=7.89711 StartY=-2.25 StartZ=0 EndX=11.7942 EndY=-4.5 EndZ=0
    g36: LineSegment StartX=11.7942 StartY=-4.5 StartZ=0 EndX=15.6913 EndY=-2.25 EndZ=0
    g37: Circle [constr] CenterX=11.7942 CenterY=0 CenterZ=0 NormalX=0 NormalY=0 NormalZ=1 AngleXU=0 Radius=4.5
    g38: LineSegment StartX=17.6913 StartY=-13.5 StartZ=0 EndX=21.5885 EndY=-11.25 EndZ=0
    g39: LineSegment StartX=21.5885 StartY=-11.25 StartZ=0 EndX=21.5885 EndY=-6.75 EndZ=0
    g40: LineSegment StartX=21.5885 StartY=-6.75 StartZ=0 EndX=17.6913 EndY=-4.5 EndZ=0
    g41: LineSegment StartX=17.6913 StartY=-4.5 StartZ=0 EndX=13.7942 EndY=-6.75 EndZ=0
    g42: LineSegment StartX=13.7942 StartY=-6.75 StartZ=0 EndX=13.7942 EndY=-11.25 EndZ=0
    g43: LineSegment StartX=13.7942 StartY=-11.25 StartZ=0 EndX=17.6913 EndY=-13.5 EndZ=0
    g44: Circle [constr] CenterX=17.6913 CenterY=-9 CenterZ=0 NormalX=0 NormalY=0 NormalZ=1 AngleXU=0 Radius=4.5
    g45: LineSegment StartX=-17.6913 StartY=-13.5 StartZ=0 EndX=-13.7942 EndY=-11.25 EndZ=0
    g46: LineSegment StartX=-13.7942 StartY=-11.25 StartZ=0 EndX=-13.7942 EndY=-6.75 EndZ=0
    g47: LineSegment StartX=-13.7942 StartY=-6.75 StartZ=0 EndX=-17.6913 EndY=-4.5 EndZ=0
    g48: LineSegment StartX=-17.6913 StartY=-4.5 StartZ=0 EndX=-21.5885 EndY=-6.75 EndZ=0
    g49: LineSegment StartX=-21.5885 StartY=-6.75 StartZ=0 EndX=-21.5885 EndY=-11.25 EndZ=0
    g50: LineSegment StartX=-21.5885 StartY=-11.25 StartZ=0 EndX=-17.6913 EndY=-13.5 EndZ=0
    g51: Circle [constr] CenterX=-17.6913 CenterY=-9 CenterZ=0 NormalX=0 NormalY=0 NormalZ=1 AngleXU=0 Radius=4.5
  constraints (122):
    c: Horizontal(g0,g2)
    c: Horizontal(g1,g2)
    c: DistanceY(g-1,g2) = 7.5
    c: Diameter(g2) = 2.2
    c: Diameter(g1) = 3
    c: Equal(g1,g0)
    c: DistanceX(g1,g0) = 7.5
    c: DistanceX(g0,g2) = 7.5
    c: DistanceX(g2,g-1) = 1
    c: Coincident(g3,g4)
    c: Coincident(g4,g5)
    c: Coincident(g5,g6)
    c: Coincident(g6,g7)
    c: Coincident(g7,g8)
    c: Coincident(g8,g3)
    c: Equal(g3, g4-g8) x5
    c: PointOnObject(g3,g9)
    c: PointOnObject(g4,g9)
    c: PointOnObject(g5,g9)
    c: PointOnObject(g6,g9)
    c: PointOnObject(g7,g9)
    c: PointOnObject(g8,g9)
    c: Coincident(g9,g-1)
    c: Vertical(g3)
    c: DistanceY(g3,g3) = 4.5
    c: Coincident(g10,g11)
    c: Coincident(g11,g12)
    c: Coincident(g12,g13)
    c: Coincident(g13,g14)
    c: Coincident(g14,g15)
    c: Coincident(g15,g10)
    c: Equal(g10, g11-g15) x5
    c: PointOnObject(g10,g16)
    c: PointOnObject(g11,g16)
    c: PointOnObject(g12,g16)
    c: PointOnObject(g13,g16)
    c: PointOnObject(g14,g16)
    c: PointOnObject(g15,g16)
    c: PointOnObject(g16,g-1)
    c: Coincident(g17,g18)
    c: Coincident(g18,g19)
    c: Coincident(g19,g20)
    c: Coincident(g20,g21)
    c: Coincident(g21,g22)
    c: Coincident(g22,g17)
    c: Equal(g17, g18-g22) x5
    c: PointOnObject(g17,g23)
    c: PointOnObject(g18,g23)
    c: PointOnObject(g19,g23)
    c: PointOnObject(g20,g23)
    c: PointOnObject(g21,g23)
    c: PointOnObject(g22,g23)
    c: Coincident(g24,g25)
    c: Coincident(g25,g26)
    c: Coincident(g26,g27)
    c: Coincident(g27,g28)
    c: Coincident(g28,g29)
    c: Coincident(g29,g24)
    c: Equal(g24, g25-g29) x5
    c: PointOnObject(g24,g30)
    c: PointOnObject(g25,g30)
    c: PointOnObject(g26,g30)
    c: PointOnObject(g27,g30)
    c: PointOnObject(g28,g30)
    c: PointOnObject(g29,g30)
    c: Coincident(g31,g32)
    c: Coincident(g32,g33)
    c: Coincident(g33,g34)
    c: Coincident(g34,g35)
    c: Coincident(g35,g36)
    c: Coincident(g36,g31)
    c: Equal(g31, g32-g36) x5
    c: PointOnObject(g31,g37)
    c: PointOnObject(g32,g37)
    c: PointOnObject(g33,g37)
    c: PointOnObject(g34,g37)
    c: PointOnObject(g35,g37)
    c: PointOnObject(g36,g37)
    c: Symmetric(g37,g23,g9)
    c: Symmetric(g16,g30,g9)
    c: Symmetric(g16,g9,g37)
    c: Vertical(g17)
    c: Vertical(g24)
    c: Equal(g17,g3)
    c: Equal(g24,g3)
    c: Equal(g31,g3)
    c: Vertical(g31)
    c: Vertical(g10)
    c: Equal(g10,g3)
    c: Distance(g6,g17) = 4
    c: Coincident(g38,g39)
    c: Coincident(g39,g40)
    c: Coincident(g40,g41)
    c: Coincident(g41,g42)
    c: Coincident(g42,g43)
    c: Coincident(g43,g38)
    c: Equal(g38, g39-g43) x5
    c: PointOnObject(g38,g44)
    c: PointOnObject(g39,g44)
    c: PointOnObject(g40,g44)
    c: PointOnObject(g41,g44)
    c: PointOnObject(g42,g44)
    c: PointOnObject(g43,g44)
    c: Vertical(g39)
    c: Equal(g39,g3)
    c: Coincident(g45,g46)
    c: Coincident(g46,g47)
    c: Coincident(g47,g48)
    c: Coincident(g48,g49)
    c: Coincident(g49,g50)
    c: Coincident(g50,g45)
    c: Equal(g45, g46-g50) x5
    c: PointOnObject(g45,g51)
    c: PointOnObject(g46,g51)
    c: PointOnObject(g47,g51)
    c: PointOnObject(g48,g51)
    c: PointOnObject(g49,g51)
    c: PointOnObject(g50,g51)
    c: Vertical(g46)
    c: Symmetric(g44,g51,g-2)
    c: Symmetric(g28,g21,g47)
    c: Equal(g46,g3)
FEATURE [PartDesign::Pocket] Pocket041
  BaseFeature = -> Pocket040
  Direction = (0,0,1)
  Length = 5
  Length2 = 5
  Profile = -> Sketch103
  ReferenceAxis = -> Sketch103 [N_Axis]
  SideType = 0
  Suppressed = false
  Type = 2
  Type2 = 0
FEATURE [PartDesign::Chamfer] Chamfer013
  Angle = 45
  Base = -> Pocket041 [Edge56,Edge57]
  BaseFeature = -> Pocket041
  ChamferType = 0
  FlipDirection = false
  Refine = true
  Size = 2
  Size2 = 1
  SupportTransform = false
  Suppressed = false
  UseAllEdges = false
FEATURE [Sketcher::SketchObject] Sketch104
  ArcFitTolerance = 1e-06
  AttachmentSupport = -> [Pocket041]
  ExternalTypes = [0]
  FullyConstrained = true
  MakeInternals = false
  MapMode = 5
  Placement = pos=(0,20,0) rot=(0,0.707107,0.707107;3.14159rad)
  _ExternalGeoVersion = 0
  sketch-geometry (112):
    g0: LineSegment StartX=-6 StartY=20 StartZ=0 EndX=-2.5359 EndY=22 EndZ=0
    g1: LineSegment StartX=-2.5359 StartY=22 StartZ=0 EndX=-2.5359 EndY=26 EndZ=0
    g2: LineSegment StartX=-2.5359 StartY=26 StartZ=0 EndX=-6 EndY=28 EndZ=0
    g3: LineSegment StartX=-6 StartY=28 StartZ=0 EndX=-9.4641 EndY=26 EndZ=0
    g4: LineSegment StartX=-9.4641 StartY=26 StartZ=0 EndX=-9.4641 EndY=22 EndZ=0
    g5: LineSegment StartX=-9.4641 StartY=22 StartZ=0 EndX=-6 EndY=20 EndZ=0
    g6: Circle [constr] CenterX=-6 CenterY=24 CenterZ=0 NormalX=0 NormalY=0 NormalZ=1 AngleXU=0 Radius=4
    g7: LineSegment StartX=-16.1782 StartY=20 StartZ=0 EndX=-12.7141 EndY=22 EndZ=0
    g8: LineSegment StartX=-12.7141 StartY=22 StartZ=0 EndX=-12.7141 EndY=26 EndZ=0
    g9: LineSegment StartX=-12.7141 StartY=26 StartZ=0 EndX=-16.1782 EndY=28 EndZ=0
    g10: LineSegment StartX=-16.1782 StartY=28 StartZ=0 EndX=-19.6423 EndY=26 EndZ=0
    g11: LineSegment StartX=-19.6423 StartY=26 StartZ=0 EndX=-19.6423 EndY=22 EndZ=0
    g12: LineSegment StartX=-19.6423 StartY=22 StartZ=0 EndX=-16.1782 EndY=20 EndZ=0
    g13: Circle [constr] CenterX=-16.1782 CenterY=24 CenterZ=0 NormalX=0 NormalY=0 NormalZ=1 AngleXU=0 Radius=4
    g14: LineSegment StartX=17 StartY=20 StartZ=0 EndX=20.4641 EndY=22 EndZ=0
    g15: LineSegment StartX=20.4641 StartY=22 StartZ=0 EndX=20.4641 EndY=26 EndZ=0
    g16: LineSegment StartX=20.4641 StartY=26 StartZ=0 EndX=17 EndY=28 EndZ=0
    g17: LineSegment StartX=17 StartY=28 StartZ=0 EndX=13.5359 EndY=26 EndZ=0
    g18: LineSegment StartX=13.5359 StartY=26 StartZ=0 EndX=13.5359 EndY=22 EndZ=0
    g19: LineSegment StartX=13.5359 StartY=22 StartZ=0 EndX=17 EndY=20 EndZ=0
    g20: Circle [constr] CenterX=17 CenterY=24 CenterZ=0 NormalX=0 NormalY=0 NormalZ=1 AngleXU=0 Radius=4
    g21: LineSegment StartX=26.5282 StartY=20 StartZ=0 EndX=29.9923 EndY=22 EndZ=0
    g22: LineSegment StartX=29.9923 StartY=22 StartZ=0 EndX=29.9923 EndY=26 EndZ=0
    g23: LineSegment StartX=29.9923 StartY=26 StartZ=0 EndX=26.5282 EndY=28 EndZ=0
    g24: LineSegment StartX=26.5282 StartY=28 StartZ=0 EndX=23.0641 EndY=26 EndZ=0
    g25: LineSegment StartX=23.0641 StartY=26 StartZ=0 EndX=23.0641 EndY=22 EndZ=0
    g26: LineSegment StartX=23.0641 StartY=22 StartZ=0 EndX=26.5282 EndY=20 EndZ=0
    g27: Circle [constr] CenterX=26.5282 CenterY=24 CenterZ=0 NormalX=0 NormalY=0 NormalZ=1 AngleXU=0 Radius=4
    g28: LineSegment StartX=21.7641 StartY=12 StartZ=0 EndX=25.2282 EndY=14 EndZ=0
    g29: LineSegment StartX=25.2282 StartY=14 StartZ=0 EndX=25.2282 EndY=18 EndZ=0
    g30: LineSegment StartX=25.2282 StartY=18 StartZ=0 EndX=21.7641 EndY=20 EndZ=0
    g31: LineSegment StartX=21.7641 StartY=20 StartZ=0 EndX=18.3 EndY=18 EndZ=0
    g32: LineSegment StartX=18.3 StartY=18 StartZ=0 EndX=18.3 EndY=14 EndZ=0
    g33: LineSegment StartX=18.3 StartY=14 StartZ=0 EndX=21.7641 EndY=12 EndZ=0
    g34: Circle [constr] CenterX=21.7641 CenterY=16 CenterZ=0 NormalX=0 NormalY=0 NormalZ=1 AngleXU=0 Radius=4
    g35: LineSegment StartX=17 StartY=4 StartZ=0 EndX=20.4641 EndY=6 EndZ=0
    g36: LineSegment StartX=20.4641 StartY=6 StartZ=0 EndX=20.4641 EndY=10 EndZ=0
    g37: LineSegment StartX=20.4641 StartY=10 StartZ=0 EndX=17 EndY=12 EndZ=0
    g38: LineSegment StartX=17 StartY=12 StartZ=0 EndX=13.5359 EndY=10 EndZ=0
    g39: LineSegment StartX=13.5359 StartY=10 StartZ=0 EndX=13.5359 EndY=6 EndZ=0
    g40: LineSegment StartX=13.5359 StartY=6 StartZ=0 EndX=17 EndY=4 EndZ=0
    g41: Circle [constr] CenterX=17 CenterY=8 CenterZ=0 NormalX=0 NormalY=0 NormalZ=1 AngleXU=0 Radius=4
    g42: LineSegment StartX=26.5282 StartY=4 StartZ=0 EndX=29.9923 EndY=6 EndZ=0
    g43: LineSegment StartX=29.9923 StartY=6 StartZ=0 EndX=29.9923 EndY=10 EndZ=0
    g44: LineSegment StartX=29.9923 StartY=10 StartZ=0 EndX=26.5282 EndY=12 EndZ=0
    g45: LineSegment StartX=26.5282 StartY=12 StartZ=0 EndX=23.0641 EndY=10 EndZ=0
    g46: LineSegment StartX=23.0641 StartY=10 StartZ=0 EndX=23.0641 EndY=6 EndZ=0
    g47: LineSegment StartX=23.0641 StartY=6 StartZ=0 EndX=26.5282 EndY=4 EndZ=0
    g48: Circle [constr] CenterX=26.5282 CenterY=8 CenterZ=0 NormalX=0 NormalY=0 NormalZ=1 AngleXU=0 Radius=4
    g49: LineSegment StartX=-11.0891 StartY=12 StartZ=0 EndX=-7.625 EndY=14 EndZ=0
    g50: LineSegment StartX=-7.625 StartY=14 StartZ=0 EndX=-7.625 EndY=18 EndZ=0
    g51: LineSegment StartX=-7.625 StartY=18 StartZ=0 EndX=-11.0891 EndY=20 EndZ=0
    g52: LineSegment StartX=-11.0891 StartY=20 StartZ=0 EndX=-14.5532 EndY=18 EndZ=0
    g53: LineSegment StartX=-14.5532 StartY=18 StartZ=0 EndX=-14.5532 EndY=14 EndZ=0
    g54: LineSegment StartX=-14.5532 StartY=14 StartZ=0 EndX=-11.0891 EndY=12 EndZ=0
    g55: Circle [constr] CenterX=-11.0891 CenterY=16 CenterZ=0 NormalX=0 NormalY=0 NormalZ=1 AngleXU=0 Radius=4
    g56: LineSegment StartX=-21.2673 StartY=12 StartZ=0 EndX=-17.8032 EndY=14 EndZ=0
    g57: LineSegment StartX=-17.8032 StartY=14 StartZ=0 EndX=-17.8032 EndY=18 EndZ=0
    g58: LineSegment StartX=-17.8032 StartY=18 StartZ=0 EndX=-21.2673 EndY=20 EndZ=0
    g59: LineSegment StartX=-21.2673 StartY=20 StartZ=0 EndX=-24.7314 EndY=18 EndZ=0
    g60: LineSegment StartX=-24.7314 StartY=18 StartZ=0 EndX=-24.7314 EndY=14 EndZ=0
    g61: LineSegment StartX=-24.7314 StartY=14 StartZ=0 EndX=-21.2673 EndY=12 EndZ=0
    g62: Circle [constr] CenterX=-21.2673 CenterY=16 CenterZ=0 NormalX=0 NormalY=0 NormalZ=1 AngleXU=0 Radius=4
    g63: LineSegment StartX=-6 StartY=4 StartZ=0 EndX=-2.5359 EndY=6 EndZ=0
    g64: LineSegment StartX=-2.5359 StartY=6 StartZ=0 EndX=-2.5359 EndY=10 EndZ=0
    g65: LineSegment StartX=-2.5359 StartY=10 StartZ=0 EndX=-6 EndY=12 EndZ=0
    g66: LineSegment StartX=-6 StartY=12 StartZ=0 EndX=-9.4641 EndY=10 EndZ=0
    g67: LineSegment StartX=-9.4641 StartY=10 StartZ=0 EndX=-9.4641 EndY=6 EndZ=0
    g68: LineSegment StartX=-9.4641 StartY=6 StartZ=0 EndX=-6 EndY=4 EndZ=0
    g69: Circle [constr] CenterX=-6 CenterY=8 CenterZ=0 NormalX=0 NormalY=0 NormalZ=1 AngleXU=0 Radius=4
    g70: LineSegment StartX=-16.1782 StartY=4 StartZ=0 EndX=-12.7141 EndY=6 EndZ=0
    g71: LineSegment StartX=-12.7141 StartY=6 StartZ=0 EndX=-12.7141 EndY=10 EndZ=0
    g72: LineSegment StartX=-12.7141 StartY=10 StartZ=0 EndX=-16.1782 EndY=12 EndZ=0
    g73: LineSegment StartX=-16.1782 StartY=12 StartZ=0 EndX=-19.6423 EndY=10 EndZ=0
    g74: LineSegment StartX=-19.6423 StartY=10 StartZ=0 EndX=-19.6423 EndY=6 EndZ=0
    g75: LineSegment StartX=-19.6423 StartY=6 StartZ=0 EndX=-16.1782 EndY=4 EndZ=0
    g76: Circle [constr] CenterX=-16.1782 CenterY=8 CenterZ=0 NormalX=0 NormalY=0 NormalZ=1 AngleXU=0 Radius=4
    g77: LineSegment StartX=-26.3564 StartY=4 StartZ=0 EndX=-22.8923 EndY=6 EndZ=0
    g78: LineSegment StartX=-22.8923 StartY=6 StartZ=0 EndX=-22.8923 EndY=10 EndZ=0
    g79: LineSegment StartX=-22.8923 StartY=10 StartZ=0 EndX=-26.3564 EndY=12 EndZ=0
    g80: LineSegment StartX=-26.3564 StartY=12 StartZ=0 EndX=-29.8205 EndY=10 EndZ=0
    g81: LineSegment StartX=-29.8205 StartY=10 StartZ=0 EndX=-29.8205 EndY=6 EndZ=0
    g82: LineSegment StartX=-29.8205 StartY=6 StartZ=0 EndX=-26.3564 EndY=4 EndZ=0
    g83: Circle [constr] CenterX=-26.3564 CenterY=8 CenterZ=0 NormalX=0 NormalY=0 NormalZ=1 AngleXU=0 Radius=4
    g84: LineSegment StartX=-26.3564 StartY=20 StartZ=0 EndX=-22.8923 EndY=22 EndZ=0
    g85: LineSegment StartX=-22.8923 StartY=22 StartZ=0 EndX=-22.8923 EndY=26 EndZ=0
    g86: LineSegment StartX=-22.8923 StartY=26 StartZ=0 EndX=-26.3564 EndY=28 EndZ=0
    g87: LineSegment StartX=-26.3564 StartY=28 StartZ=0 EndX=-29.8205 EndY=26 EndZ=0
    g88: LineSegment StartX=-29.8205 StartY=26 StartZ=0 EndX=-29.8205 EndY=22 EndZ=0
    g89: LineSegment StartX=-29.8205 StartY=22 StartZ=0 EndX=-26.3564 EndY=20 EndZ=0
    g90: Circle [constr] CenterX=-26.3564 CenterY=24 CenterZ=0 NormalX=0 NormalY=0 NormalZ=1 AngleXU=0 Radius=4
    g91: LineSegment StartX=21.7641 StartY=28 StartZ=0 EndX=25.2282 EndY=30 EndZ=0
    g92: LineSegment StartX=25.2282 StartY=30 StartZ=0 EndX=25.2282 EndY=34 EndZ=0
    g93: LineSegment StartX=25.2282 StartY=34 StartZ=0 EndX=21.7641 EndY=36 EndZ=0
    g94: LineSegment StartX=21.7641 StartY=36 StartZ=0 EndX=18.3 EndY=34 EndZ=0
    g95: LineSegment StartX=18.3 StartY=34 StartZ=0 EndX=18.3 EndY=30 EndZ=0
    g96: LineSegment StartX=18.3 StartY=30 StartZ=0 EndX=21.7641 EndY=28 EndZ=0
    g97: Circle [constr] CenterX=21.7641 CenterY=32 CenterZ=0 NormalX=0 NormalY=0 NormalZ=1 AngleXU=0 Radius=4
    g98: LineSegment StartX=-11.0891 StartY=28 StartZ=0 EndX=-7.625 EndY=30 EndZ=0
    g99: LineSegment StartX=-7.625 StartY=30 StartZ=0 EndX=-7.625 EndY=34 EndZ=0
    g100: LineSegment StartX=-7.625 StartY=34 StartZ=0 EndX=-11.0891 EndY=36 EndZ=0
    g101: LineSegment StartX=-11.0891 StartY=36 StartZ=0 EndX=-14.5532 EndY=34 EndZ=0
    g102: LineSegment StartX=-14.5532 StartY=34 StartZ=0 EndX=-14.5532 EndY=30 EndZ=0
    g103: LineSegment StartX=-14.5532 StartY=30 StartZ=0 EndX=-11.0891 EndY=28 EndZ=0
    g104: Circle [constr] CenterX=-11.0891 CenterY=32 CenterZ=0 NormalX=0 NormalY=0 NormalZ=1 AngleXU=0 Radius=4
    g105: LineSegment StartX=-21.2673 StartY=28 StartZ=0 EndX=-17.8032 EndY=30 EndZ=0
    g106: LineSegment StartX=-17.8032 StartY=30 StartZ=0 EndX=-17.8032 EndY=34 EndZ=0
    g107: LineSegment StartX=-17.8032 StartY=34 StartZ=0 EndX=-21.2673 EndY=36 EndZ=0
    g108: LineSegment StartX=-21.2673 StartY=36 StartZ=0 EndX=-24.7314 EndY=34 EndZ=0
    g109: LineSegment StartX=-24.7314 StartY=34 StartZ=0 EndX=-24.7314 EndY=30 EndZ=0
    g110: LineSegment StartX=-24.7314 StartY=30 StartZ=0 EndX=-21.2673 EndY=28 EndZ=0
    g111: Circle [constr] CenterX=-21.2673 CenterY=32 CenterZ=0 NormalX=0 NormalY=0 NormalZ=1 AngleXU=0 Radius=4
  constraints (262):
    c: Coincident(g0,g1)
    c: Coincident(g1,g2)
    c: Coincident(g2,g3)
    c: Coincident(g3,g4)
    c: Coincident(g4,g5)
    c: Coincident(g5,g0)
    c: Equal(g0, g1-g5) x5
    c: PointOnObject(g0,g6)
    c: PointOnObject(g1,g6)
    c: PointOnObject(g2,g6)
    c: PointOnObject(g3,g6)
    c: PointOnObject(g4,g6)
    c: PointOnObject(g5,g6)
    c: Coincident(g7,g8)
    c: Coincident(g8,g9)
    c: Coincident(g9,g10)
    c: Coincident(g10,g11)
    c: Coincident(g11,g12)
    c: Coincident(g12,g7)
    c: Equal(g7, g8-g12) x5
    c: PointOnObject(g7,g13)
    c: PointOnObject(g8,g13)
    c: PointOnObject(g9,g13)
    c: PointOnObject(g10,g13)
    c: PointOnObject(g11,g13)
    c: PointOnObject(g12,g13)
    c: Coincident(g14,g15)
    c: Coincident(g15,g16)
    c: Coincident(g16,g17)
    c: Coincident(g17,g18)
    c: Coincident(g18,g19)
    c: Coincident(g19,g14)
    c: Equal(g14, g15-g19) x5
    c: PointOnObject(g14,g20)
    c: PointOnObject(g15,g20)
    c: PointOnObject(g16,g20)
    c: PointOnObject(g17,g20)
    c: PointOnObject(g18,g20)
    c: PointOnObject(g19,g20)
    c: Coincident(g21,g22)
    c: Coincident(g22,g23)
    c: Coincident(g23,g24)
    c: Coincident(g24,g25)
    c: Coincident(g25,g26)
    c: Coincident(g26,g21)
    c: Equal(g21, g22-g26) x5
    c: PointOnObject(g21,g27)
    c: PointOnObject(g22,g27)
    c: PointOnObject(g23,g27)
    c: PointOnObject(g24,g27)
    c: PointOnObject(g25,g27)
    c: PointOnObject(g26,g27)
    c: Coincident(g28,g29)
    c: Coincident(g29,g30)
    c: Coincident(g30,g31)
    c: Coincident(g31,g32)
    c: Coincident(g32,g33)
    c: Coincident(g33,g28)
    c: Equal(g28, g29-g33) x5
    c: PointOnObject(g28,g34)
    c: PointOnObject(g29,g34)
    c: PointOnObject(g30,g34)
    c: PointOnObject(g31,g34)
    c: PointOnObject(g32,g34)
    c: PointOnObject(g33,g34)
    c: Vertical(g29)
    c: Vertical(g8)
    c: Vertical(g1)
    c: Vertical(g15)
    c: Vertical(g22)
    c: Coincident(g35,g36)
    c: Coincident(g36,g37)
    c: Coincident(g37,g38)
    c: Coincident(g38,g39)
    c: Coincident(g39,g40)
    c: Coincident(g40,g35)
    c: Equal(g35, g36-g40) x5
    c: PointOnObject(g35,g41)
    c: PointOnObject(g36,g41)
    c: PointOnObject(g37,g41)
    c: PointOnObject(g38,g41)
    c: PointOnObject(g39,g41)
    c: PointOnObject(g40,g41)
    c: Coincident(g42,g43)
    c: Coincident(g43,g44)
    c: Coincident(g44,g45)
    c: Coincident(g45,g46)
    c: Coincident(g46,g47)
    c: Coincident(g47,g42)
    c: Equal(g42, g43-g47) x5
    c: PointOnObject(g42,g48)
    c: PointOnObject(g43,g48)
    c: PointOnObject(g44,g48)
    c: PointOnObject(g45,g48)
    c: PointOnObject(g46,g48)
    c: PointOnObject(g47,g48)
    c: Coincident(g49,g50)
    c: Coincident(g50,g51)
    c: Coincident(g51,g52)
    c: Coincident(g52,g53)
    c: Coincident(g53,g54)
    c: Coincident(g54,g49)
    c: Equal(g49, g50-g54) x5
    c: PointOnObject(g49,g55)
    c: PointOnObject(g50,g55)
    c: PointOnObject(g51,g55)
    c: PointOnObject(g52,g55)
    c: PointOnObject(g53,g55)
    c: PointOnObject(g54,g55)
    c: Coincident(g56,g57)
    c: Coincident(g57,g58)
    c: Coincident(g58,g59)
    c: Coincident(g59,g60)
    c: Coincident(g60,g61)
    c: Coincident(g61,g56)
    c: Equal(g56, g57-g61) x5
    c: PointOnObject(g56,g62)
    c: PointOnObject(g57,g62)
    c: PointOnObject(g58,g62)
    c: PointOnObject(g59,g62)
    c: PointOnObject(g60,g62)
    c: PointOnObject(g61,g62)
    c: Coincident(g63,g64)
    c: Coincident(g64,g65)
    c: Coincident(g65,g66)
    c: Coincident(g66,g67)
    c: Coincident(g67,g68)
    c: Coincident(g68,g63)
    c: Equal(g63, g64-g68) x5
    c: PointOnObject(g63,g69)
    c: PointOnObject(g64,g69)
    c: PointOnObject(g65,g69)
    c: PointOnObject(g66,g69)
    c: PointOnObject(g67,g69)
    c: PointOnObject(g68,g69)
    c: Coincident(g70,g71)
    c: Coincident(g71,g72)
    c: Coincident(g72,g73)
    c: Coincident(g73,g74)
    c: Coincident(g74,g75)
    c: Coincident(g75,g70)
    c: Equal(g70, g71-g75) x5
    c: PointOnObject(g70,g76)
    c: PointOnObject(g71,g76)
    c: PointOnObject(g72,g76)
    c: PointOnObject(g73,g76)
    c: PointOnObject(g74,g76)
    c: PointOnObject(g75,g76)
    c: Coincident(g77,g78)
    c: Coincident(g78,g79)
    c: Coincident(g79,g80)
    c: Coincident(g80,g81)
    c: Coincident(g81,g82)
    c: Coincident(g82,g77)
    c: Equal(g77, g78-g82) x5
    c: PointOnObject(g77,g83)
    c: PointOnObject(g78,g83)
    c: PointOnObject(g79,g83)
    c: PointOnObject(g80,g83)
    c: PointOnObject(g81,g83)
    c: PointOnObject(g82,g83)
    c: Coincident(g84,g85)
    c: Coincident(g85,g86)
    c: Coincident(g86,g87)
    c: Coincident(g87,g88)
    c: Coincident(g88,g89)
    c: Coincident(g89,g84)
    c: Equal(g84, g85-g89) x5
    c: PointOnObject(g84,g90)
    c: PointOnObject(g85,g90)
    c: PointOnObject(g86,g90)
    c: PointOnObject(g87,g90)
    c: PointOnObject(g88,g90)
    c: PointOnObject(g89,g90)
    c: Symmetric(g79,g72,g56)
    c: Vertical(g57)
    c: Vertical(g50)
    c: Vertical(g64)
    c: Vertical(g71)
    c: Vertical(g78)
    c: Vertical(g85)
    c: Symmetric(g90,g6,g13)
    c: DistanceY(g85,g85) = 4
    c: Equal(g85,g8)
    c: Equal(g85,g1)
    c: Horizontal(g90,g13)
    c: Symmetric(g84,g7,g58)
    c: Equal(g85,g57)
    c: Equal(g85,g50)
    c: Symmetric(g7,g0,g51)
    c: Symmetric(g72,g65,g49)
    c: Equal(g85,g71)
    c: Equal(g78,g85)
    c: Horizontal(g83,g76)
    c: Equal(g85,g64)
    c: Symmetric(g14,g21,g30)
    c: Symmetric(g37,g44,g28)
    c: Horizontal(g20,g27)
    c: Horizontal(g41,g48)
    c: Horizontal(g6,g20)
    c: Distance(g11,g85) = 3.25
    c: Vertical(g83,g90)
    c: Vertical(g41,g20)
    c: Distance(g25,g15) = 2.6
    c: Vertical(g43)
    c: Vertical(g36)
    c: Equal(g85,g15)
    c: Equal(g85,g22)
    c: Equal(g85,g29)
    c: Equal(g85,g36)
    c: Equal(g85,g43)
    c: Distance(g69,g-1) = 8
    c: Distance(g69,g-2) = 6
    c: Distance(g41,g-2) = 17
    c: Coincident(g91,g92)
    c: Coincident(g92,g93)
    c: Coincident(g93,g94)
    c: Coincident(g94,g95)
    c: Coincident(g95,g96)
    c: Coincident(g96,g91)
    c: Equal(g91, g92-g96) x5
    c: PointOnObject(g91,g97)
    c: PointOnObject(g92,g97)
    c: PointOnObject(g93,g97)
    c: PointOnObject(g94,g97)
    c: PointOnObject(g95,g97)
    c: PointOnObject(g96,g97)
    c: Coincident(g98,g99)
    c: Coincident(g99,g100)
    c: Coincident(g100,g101)
    c: Coincident(g101,g102)
    c: Coincident(g102,g103)
    c: Coincident(g103,g98)
    c: Equal(g98, g99-g103) x5
    c: PointOnObject(g98,g104)
    c: PointOnObject(g99,g104)
    c: PointOnObject(g100,g104)
    c: PointOnObject(g101,g104)
    c: PointOnObject(g102,g104)
    c: PointOnObject(g103,g104)
    c: Coincident(g105,g106)
    c: Coincident(g106,g107)
    c: Coincident(g107,g108)
    c: Coincident(g108,g109)
    c: Coincident(g109,g110)
    c: Coincident(g110,g105)
    c: Equal(g105, g106-g110) x5
    c: PointOnObject(g105,g111)
    c: PointOnObject(g106,g111)
    c: PointOnObject(g107,g111)
    c: PointOnObject(g108,g111)
    c: PointOnObject(g109,g111)
    c: PointOnObject(g110,g111)
    c: Vertical(g106)
    c: Vertical(g99)
    c: Vertical(g92)
    c: Equal(g85,g109)
    c: Equal(g85,g102)
    c: Equal(g85,g95)
    c: Symmetric(g23,g16,g91)
    c: Symmetric(g9,g2,g98)
    c: Symmetric(g86,g9,g105)
FEATURE [PartDesign::Pocket] Pocket042
  BaseFeature = -> Chamfer013
  Direction = (0,-1,2e-16)
  Length = 5
  Length2 = 5
  Profile = -> Sketch104
  ReferenceAxis = -> Sketch104 [N_Axis]
  SideType = 0
  Suppressed = false
  Type = 0
  Type2 = 0
FEATURE [PartDesign::Chamfer] Chamfer012
  Angle = 45
  Base = -> Pocket042 [Edge54]
  BaseFeature = -> Pocket042
  ChamferType = 0
  FlipDirection = false
  Size = 1.8
  Size2 = 1
  SupportTransform = false
  Suppressed = false
  UseAllEdges = false
FEATURE [PartDesign::Fillet] Fillet049
  Base = -> Chamfer012 [Edge4,Edge65,Edge63,Edge195,Edge146,Edge107,Edge101]
  BaseFeature = -> Chamfer012
  Radius = 1.4
  Refine = true
  SupportTransform = false
  Suppressed = false
  UseAllEdges = false
FEATURE [Sketcher::SketchObject] Sketch105
  ArcFitTolerance = 1e-06
  AttachmentSupport = -> [Pad085]
  ExternalTypes = [0]
  FullyConstrained = true
  MakeInternals = false
  MapMode = 5
  Placement = pos=(0,0,3) rot=(0,0,1;0rad)
  _ExternalGeoVersion = 1
  sketch-geometry (4):
    g0: LineSegment StartX=-30 StartY=-11.5 StartZ=0 EndX=-28 EndY=-11.5 EndZ=0
    g1: LineSegment StartX=-28 StartY=-11.5 StartZ=0 EndX=-28 EndY=-10.5 EndZ=0
    g2: LineSegment StartX=-28 StartY=-10.5 StartZ=0 EndX=-30 EndY=-10.5 EndZ=0
    g3: LineSegment StartX=-30 StartY=-10.5 StartZ=0 EndX=-30 EndY=-11.5 EndZ=0
  constraints (12):
    c: Coincident(g0,g1)
    c: Coincident(g1,g2)
    c: Coincident(g2,g3)
    c: Coincident(g3,g0)
    c: Horizontal(g0)
    c: Horizontal(g2)
    c: Vertical(g1)
    c: Vertical(g3)
    c: Distance(g-1,g0) = 11.5
    c: Distance(g1,g1) = 1
    c: DistanceX(g2,g2) = 2
    c: Distance(g-2,g1) = 28
FEATURE [PartDesign::Pad] Pad087
  BaseFeature = -> Fillet049
  Direction = (0,0,1)
  Length = 5
  Length2 = 10
  Profile = -> Sketch105
  ReferenceAxis = -> Sketch105 [N_Axis]
  Refine = true
  SideType = 0
  Suppressed = false
  Type = 0
  Type2 = 0
FEATURE [PartDesign::Chamfer] Chamfer014
  Angle = 45
  Base = -> Pad087 [Edge820]
  BaseFeature = -> Pad087
  ChamferType = 0
  FlipDirection = false
  Refine = true
  Size = 0.9
  Size2 = 1
  SupportTransform = false
  Suppressed = false
  UseAllEdges = false
FEATURE [PartDesign::Chamfer] Chamfer015
  Angle = 45
  Base = -> Chamfer014 [Edge84]
  BaseFeature = -> Chamfer014
  ChamferType = 0
  FlipDirection = false
  Refine = true
  Size = 2
  Size2 = 1
  SupportTransform = false
  Suppressed = false
  UseAllEdges = false
FEATURE [Sketcher::SketchObject] Sketch106
  ArcFitTolerance = 1e-06
  ExternalTypes = [0,0]
  FullyConstrained = true
  MakeInternals = false
  MapMode = 5
  Placement = pos=(0,-20,0) rot=(1,0,0;1.5708rad)
  _ExternalGeoVersion = 1
  sketch-geometry (6):
    g0: LineSegment StartX=-32 StartY=35.25 StartZ=0 EndX=-32 EndY=36.75 EndZ=0
    g1: LineSegment StartX=-32 StartY=36.75 StartZ=0 EndX=-32.75 EndY=36.75 EndZ=0
    g2: LineSegment StartX=-32.75 StartY=36.75 StartZ=0 EndX=-32 EndY=35.25 EndZ=0
    g3: LineSegment StartX=32 StartY=35.25 StartZ=0 EndX=32 EndY=36.75 EndZ=0
    g4: LineSegment StartX=32 StartY=36.75 StartZ=0 EndX=32.75 EndY=36.75 EndZ=0
    g5: LineSegment StartX=32.75 StartY=36.75 StartZ=0 EndX=32 EndY=35.25 EndZ=0
  constraints (17):
    c: Vertical(g0)
    c: Coincident(g0,g1)
    c: Horizontal(g1)
    c: Coincident(g1,g2)
    c: Coincident(g2,g0)
    c: Vertical(g3)
    c: Coincident(g3,g4)
    c: Horizontal(g4)
    c: Coincident(g4,g5)
    c: Coincident(g5,g3)
    c: Distance(g4,g4) = 0.75
    c: DistanceY(g3,g3) = 1.5
    c: Distance(g-1,g4) = 36.75
    c: Equal(g0,g3)
    c: Equal(g4,g1)
    c: Symmetric(g3,g0,g-2)
    c: Distance(g3,g0) = 64
FEATURE [PartDesign::Pad] Pad088
  BaseFeature = -> Chamfer015
  Direction = (0,-1,2e-16)
  Length = 28
  Length2 = -12
  Profile = -> Sketch106
  ReferenceAxis = -> Sketch106 [N_Axis]
  Refine = true
  Reversed = true
  SideType = 1
  Suppressed = false
  Type = 0
  Type2 = 0
FEATURE [Sketcher::SketchObject] Sketch107
  ArcFitTolerance = 1e-06
  AttachmentSupport = -> [Pad088]
  ExternalTypes = [0]
  FullyConstrained = true
  MakeInternals = false
  MapMode = 5
  Placement = pos=(-32,0,0) rot=(0.57735,-0.57735,-0.57735;2.0944rad)
  _ExternalGeoVersion = 1
  sketch-geometry (28):
    g0: LineSegment StartX=10 StartY=24 StartZ=0 EndX=10 EndY=12 EndZ=0
    g1: LineSegment StartX=10 StartY=12 StartZ=0 EndX=9.25 EndY=12 EndZ=0
    g2: LineSegment StartX=3 StartY=14 StartZ=0 EndX=3 EndY=22 EndZ=0
    g3: LineSegment StartX=5 StartY=24 StartZ=0 EndX=8.45 EndY=24 EndZ=0
    g4: LineSegment StartX=3 StartY=22 StartZ=0 EndX=3.73483 EndY=22.7348 EndZ=0
    g5: LineSegment StartX=3 StartY=14 StartZ=0 EndX=3.73483 EndY=13.2652 EndZ=0
    g6: LineSegment StartX=9.25 StartY=12 StartZ=0 EndX=9.25 EndY=24 EndZ=0
    g7: LineSegment StartX=8.45 StartY=23.25 StartZ=0 EndX=5.31066 EndY=23.25 EndZ=0
    g8: LineSegment StartX=5.31066 StartY=23.25 StartZ=0 EndX=4.7955 EndY=22.7348 EndZ=0
    g9: LineSegment StartX=3.75 StartY=21.6893 StartZ=0 EndX=3.75 EndY=14.3107 EndZ=0
    g10: LineSegment StartX=3.75 StartY=14.3107 StartZ=0 EndX=4.26517 EndY=13.7955 EndZ=0
    g11: LineSegment StartX=5.31066 StartY=12.75 StartZ=0 EndX=8.45 EndY=12.75 EndZ=0
    g12: LineSegment StartX=8.45 StartY=24 StartZ=0 EndX=8.45 EndY=23.25 EndZ=0
    g13: LineSegment StartX=9.25 StartY=24 StartZ=0 EndX=10 EndY=24 EndZ=0
    g14: LineSegment StartX=8.45 StartY=12.75 StartZ=0 EndX=8.45 EndY=12 EndZ=0
    g15: LineSegment StartX=8.45 StartY=12 StartZ=0 EndX=5 EndY=12 EndZ=0
    g16: LineSegment StartX=3.73483 StartY=13.2652 StartZ=0 EndX=4.26517 EndY=13.7955 EndZ=0
    g17: LineSegment StartX=4.26517 StartY=12.7348 StartZ=0 EndX=4.7955 EndY=13.2652 EndZ=0
    g18: LineSegment StartX=4.26517 StartY=12.7348 StartZ=0 EndX=5 EndY=12 EndZ=0
    g19: LineSegment StartX=4.7955 StartY=13.2652 StartZ=0 EndX=5.31066 EndY=12.75 EndZ=0
    g20: LineSegment [constr] StartX=3.73483 StartY=13.2652 StartZ=0 EndX=4.26517 EndY=12.7348 EndZ=0
    g21: LineSegment [constr] StartX=4.26517 StartY=13.7955 StartZ=0 EndX=4.7955 EndY=13.2652 EndZ=0
    g22: LineSegment StartX=3.73483 StartY=22.7348 StartZ=0 EndX=4.26517 EndY=22.2045 EndZ=0
    g23: LineSegment StartX=4.26517 StartY=23.2652 StartZ=0 EndX=4.7955 EndY=22.7348 EndZ=0
    g24: LineSegment StartX=4.26517 StartY=23.2652 StartZ=0 EndX=5 EndY=24 EndZ=0
    g25: LineSegment StartX=4.26517 StartY=22.2045 StartZ=0 EndX=3.75 EndY=21.6893 EndZ=0
    g26: LineSegment [constr] StartX=3.73483 StartY=22.7348 StartZ=0 EndX=4.26517 EndY=23.2652 EndZ=0
    g27: LineSegment [constr] StartX=4.26517 StartY=22.2045 StartZ=0 EndX=4.7955 EndY=22.7348 EndZ=0
  constraints (80):
    c: Vertical(g0)
    c: Coincident(g0,g1)
    c: Vertical(g2)
    c: Coincident(g13,g0)
    c: Distance(g-2,g0) = 10
    c: Distance(g0,g2) = 7
    c: DistanceY(g0,g0) = 12
    c: DistanceY(g2,g2) = 8
    c: Coincident(g4,g2)
    c: Coincident(g24,g3)
    c: Coincident(g5,g2)
    c: Angle(g5,g4) = 1.5708
    c: Coincident(g18,g15)
    c: Vertical(g6)
    c: Coincident(g7,g8)
    c: Coincident(g25,g9)
    c: Vertical(g9)
    c: Coincident(g9,g10)
    c: Coincident(g19,g11)
    c: Distance(g0,g6) = 0.75
    c: Distance(g9,g2) = 0.75
    c: Vertical(g12)
    c: Horizontal(g3)
    c: Horizontal(g13)
    c: Coincident(g12,g3)
    c: Horizontal(g7)
    c: Coincident(g12,g7)
    c: Horizontal(g3,g13)
    c: Coincident(g13,g6)
    c: Vertical(g14)
    c: Horizontal(g11)
    c: Coincident(g14,g11)
    c: Horizontal(g1)
    c: Horizontal(g15)
    c: Distance(g-1,g15) = 12
    c: Coincident(g14,g15)
    c: Horizontal(g14,g1)
    c: Coincident(g1,g6)
    c: Distance(g6,g12) = 0.8
    c: Vertical(g11,g7)
    c: Equal(g14,g12)
    c: Equal(g12,g13)
    c: Equal(g15,g3)
    c: Coincident(g16,g5)
    c: Coincident(g17,g18)
    c: Coincident(g16,g10)
    c: Coincident(g17,g19)
    c: Parallel(g5,g10)
    c: Parallel(g5,g19)
    c: Parallel(g18,g10)
    c: Coincident(g20,g5)
    c: Coincident(g21,g10)
    c: Coincident(g21,g17)
    c: Parallel(g18,g20)
    c: Perpendicular(g5,g16)
    c: Parallel(g16,g17)
    c: Parallel(g19,g21)
    c: Equal(g1,g20)
    c: Equal(g5,g18)
    c: Coincident(g20,g17)
    c: Coincident(g22,g4)
    c: Coincident(g23,g24)
    c: Coincident(g22,g25)
    c: Coincident(g23,g8)
    c: Parallel(g8,g4)
    c: Parallel(g25,g4)
    c: Parallel(g8,g24)
    c: Coincident(g26,g4)
    c: Coincident(g26,g23)
    c: Coincident(g27,g22)
    c: Coincident(g27,g8)
    c: Perpendicular(g25,g22)
    c: Parallel(g23,g22)
    c: Parallel(g4,g26)
    c: Parallel(g25,g27)
    c: Angle(g15,g18) = 2.35619
    c: Equal(g17,g14)
    c: Equal(g12,g23)
    c: Equal(g27,g23)
    c: Equal(g4,g24)
FEATURE [PartDesign::Pocket] Pocket043
  BaseFeature = -> Pad088
  Direction = (1,0,0)
  Length = 3
  Length2 = 5
  Profile = -> Sketch107
  ReferenceAxis = -> Sketch107 [N_Axis]
  Refine = true
  SideType = 0
  Suppressed = false
  Type = 0
  Type2 = 0
FEATURE [Sketcher::SketchObject] Sketch108
  ArcFitTolerance = 1e-06
  AttachmentSupport = -> [Pad084]
  ExternalTypes = [0]
  FullyConstrained = true
  MakeInternals = false
  MapMode = 5
  Placement = pos=(0,0,40) rot=(0,0,1;0rad)
  _ExternalGeoVersion = 1
  sketch-geometry (12):
    g0: ArcOfCircle CenterX=-9.5 CenterY=9 CenterZ=0 NormalX=0 NormalY=0 NormalZ=1 AngleXU=0 Radius=4 StartAngle=1.5708 EndAngle=4.71239
    g1: ArcOfCircle CenterX=-1.5 CenterY=9 CenterZ=0 NormalX=0 NormalY=0 NormalZ=1 AngleXU=0 Radius=4 StartAngle=4.71239 EndAngle=7.85398
    g2: LineSegment StartX=-9.5 StartY=13 StartZ=0 EndX=-1.5 EndY=13 EndZ=0
    g3: LineSegment StartX=-9.5 StartY=5 StartZ=0 EndX=-1.5 EndY=5 EndZ=0
    g4: ArcOfCircle CenterX=-9.5 CenterY=9 CenterZ=0 NormalX=0 NormalY=0 NormalZ=1 AngleXU=0 Radius=3 StartAngle=1.5708 EndAngle=4.71239
    g5: ArcOfCircle CenterX=-1.5 CenterY=9 CenterZ=0 NormalX=0 NormalY=0 NormalZ=1 AngleXU=0 Radius=3 StartAngle=4.71239 EndAngle=7.85398
    g6: LineSegment StartX=-9.5 StartY=12 StartZ=0 EndX=-1.5 EndY=12 EndZ=0
    g7: LineSegment StartX=-9.5 StartY=6 StartZ=0 EndX=-1.5 EndY=6 EndZ=0
    g8: ArcOfCircle CenterX=-8 CenterY=9 CenterZ=0 NormalX=0 NormalY=0 NormalZ=1 AngleXU=0 Radius=2.1 StartAngle=1.5708 EndAngle=4.71239
    g9: ArcOfCircle CenterX=-3 CenterY=9 CenterZ=0 NormalX=0 NormalY=0 NormalZ=1 AngleXU=0 Radius=2.1 StartAngle=4.71239 EndAngle=7.85398
    g10: LineSegment StartX=-8 StartY=11.1 StartZ=0 EndX=-3 EndY=11.1 EndZ=0
    g11: LineSegment StartX=-8 StartY=6.9 StartZ=0 EndX=-3 EndY=6.9 EndZ=0
  constraints (28):
    c: Tangent(g0,g2) = 1.5708
    c: Tangent(g0,g3) = -1.5708
    c: Tangent(g1,g2) = 1.5708
    c: Tangent(g1,g3) = -1.5708
    c: Equal(g0,g1)
    c: Horizontal(g2)
    c: Radius(g1) = 4
    c: DistanceX(g2,g2) = 8
    c: Distance(g-1,g3) = 5
    c: Distance(g1,g-2) = 1.5
    c: Tangent(g4,g6) = 1.5708
    c: Tangent(g4,g7) = -1.5708
    c: Tangent(g5,g6) = 1.5708
    c: Tangent(g5,g7) = -1.5708
    c: Equal(g4,g5)
    c: Radius(g4) = 3
    c: Coincident(g4,g0)
    c: Coincident(g5,g1)
    c: Tangent(g8,g10) = 1.5708
    c: Tangent(g8,g11) = -1.5708
    c: Tangent(g9,g10) = 1.5708
    c: Tangent(g9,g11) = -1.5708
    c: Equal(g8,g9)
    c: Radius(g8) = 2.1
    c: Horizontal(g10)
    c: DistanceX(g10,g10) = 5
    c: Horizontal(g9,g1)
    c: Distance(g9,g-2) = 3
FEATURE [PartDesign::Pad] Pad089
  BaseFeature = -> Pocket043
  Direction = (0,0,1)
  Length = 1.5
  Length2 = 10
  Profile = -> Sketch108 [Edge3,Edge2,Edge4,Edge1,Edge5,Edge8,Edge6,Edge7]
  ReferenceAxis = -> Sketch108 [N_Axis]
  Refine = true
  SideType = 0
  Suppressed = false
  Type = 0
  Type2 = 0
FEATURE [PartDesign::Pad] Pad090
  BaseFeature = -> Pad089
  Direction = (0,0,1)
  Length = 2.5
  Length2 = -1.5
  Profile = -> Sketch108 [Edge11,Edge10,Edge9,Edge12,Edge4,Edge3,Edge2,Edge1]
  ReferenceAxis = -> Sketch108 [N_Axis]
  Refine = true
  SideType = 1
  Suppressed = false
  Type = 0
  Type2 = 0
FEATURE [Sketcher::SketchObject] Sketch109
  ArcFitTolerance = 1e-06
  AttachmentSupport = -> [Pad090]
  ExternalTypes = [0]
  FullyConstrained = true
  MakeInternals = false
  MapMode = 5
  Placement = pos=(0,0,42.5) rot=(0,0,1;0rad)
  _ExternalGeoVersion = 1
  sketch-geometry (11):
    g0: LineSegment StartX=-3 StartY=11.1 StartZ=0 EndX=-3 EndY=12.1 EndZ=0
    g1: LineSegment StartX=-3 StartY=12.1 StartZ=0 EndX=-8 EndY=12.1 EndZ=0
    g2: LineSegment StartX=-8 StartY=12.1 StartZ=0 EndX=-8 EndY=11.1 EndZ=0
    g3: LineSegment StartX=-8 StartY=11.1 StartZ=0 EndX=-3 EndY=11.1 EndZ=0
    g4: ArcOfCircle CenterX=-8 CenterY=9 CenterZ=0 NormalX=0 NormalY=0 NormalZ=1 AngleXU=0 Radius=2.1 StartAngle=1.5708 EndAngle=3.14159
    g5: ArcOfCircle CenterX=-3 CenterY=9 CenterZ=0 NormalX=0 NormalY=0 NormalZ=1 AngleXU=0 Radius=2.1 StartAngle=0 EndAngle=1.5708
    g6: ArcOfCircle CenterX=-3 CenterY=9 CenterZ=0 NormalX=0 NormalY=0 NormalZ=1 AngleXU=0 Radius=3.1 StartAngle=0 EndAngle=1.5708
    g7: ArcOfCircle CenterX=-8 CenterY=9 CenterZ=0 NormalX=0 NormalY=0 NormalZ=1 AngleXU=0 Radius=3.1 StartAngle=1.5708 EndAngle=3.14159
    g8: LineSegment StartX=-11.1 StartY=9 StartZ=0 EndX=-10.1 EndY=9 EndZ=0
    g9: LineSegment StartX=0.1 StartY=9 StartZ=0 EndX=-0.9 EndY=9 EndZ=0
    g10: LineSegment StartX=-10.1 StartY=9 StartZ=0 EndX=-0.9 EndY=9 EndZ=0
  constraints (32):
    c: Coincident(g0,g1)
    c: Coincident(g1,g2)
    c: Coincident(g2,g3)
    c: Coincident(g3,g0)
    c: Vertical(g0)
    c: Vertical(g2)
    c: Horizontal(g1)
    c: Horizontal(g3)
    c: Distance(g0,g2) = 5
    c: Distance(g1,g3) = 1
    c: Coincident(g4,g2)
    c: Coincident(g5,g0)
    c: Coincident(g6,g5)
    c: Coincident(g6,g0)
    c: Coincident(g7,g4)
    c: Coincident(g7,g1)
    c: Horizontal(g7,g4)
    c: Coincident(g8,g7)
    c: Coincident(g8,g4)
    c: Horizontal(g8)
    c: Coincident(g9,g6)
    c: Coincident(g9,g5)
    c: Horizontal(g9)
    c: Horizontal(g5,g5)
    c: Horizontal(g4,g5)
    c: Vertical(g2,g4)
    c: Vertical(g5,g0)
    c: Radius(g5) = 2.1
    c: Distance(g-1,g9) = 9
    c: Distance(g5,g-2) = 3
    c: Coincident(g10,g4)
    c: Coincident(g10,g5)
FEATURE [PartDesign::Pad] Pad091
  BaseFeature = -> Pad090
  Direction = (0,0,1)
  Length = 6
  Length2 = 10
  Profile = -> Sketch109 [Edge11,Edge6,Edge8,Edge9,Edge5,Edge1,Edge2,Edge3]
  ReferenceAxis = -> Sketch109 [N_Axis]
  Refine = true
  SideType = 0
  Suppressed = false
  Type = 0
  Type2 = 0
FEATURE [Sketcher::SketchObject] Sketch110
  ArcFitTolerance = 1e-06
  AttachmentSupport = -> [Pad091]
  ExternalTypes = [0]
  FullyConstrained = true
  MakeInternals = false
  MapMode = 5
  Placement = pos=(0,0,41) rot=(0,0,1;0rad)
  _ExternalGeoVersion = 1
  sketch-geometry (14):
    g0: LineSegment StartX=-8 StartY=16 StartZ=0 EndX=-8 EndY=12 EndZ=0
    g1: LineSegment StartX=-8 StartY=12 StartZ=0 EndX=-7 EndY=12 EndZ=0
    g2: LineSegment StartX=-7 StartY=12 StartZ=0 EndX=-7 EndY=16 EndZ=0
    g3: LineSegment StartX=-7 StartY=16 StartZ=0 EndX=-8 EndY=16 EndZ=0
    g4: LineSegment StartX=-6 StartY=16 StartZ=0 EndX=-6 EndY=12 EndZ=0
    g5: LineSegment StartX=-6 StartY=12 StartZ=0 EndX=-5 EndY=12 EndZ=0
    g6: LineSegment StartX=-5 StartY=12 StartZ=0 EndX=-5 EndY=16 EndZ=0
    g7: LineSegment StartX=-5 StartY=16 StartZ=0 EndX=-6 EndY=16 EndZ=0
    g8: LineSegment StartX=-4 StartY=16 StartZ=0 EndX=-4 EndY=12 EndZ=0
    g9: LineSegment StartX=-4 StartY=12 StartZ=0 EndX=-3 EndY=12 EndZ=0
    g10: LineSegment StartX=-3 StartY=12 StartZ=0 EndX=-3 EndY=16 EndZ=0
    g11: LineSegment StartX=-3 StartY=16 StartZ=0 EndX=-4 EndY=16 EndZ=0
    g12: LineSegment [constr] StartX=-7 StartY=12 StartZ=0 EndX=-6 EndY=12 EndZ=0
    g13: LineSegment [constr] StartX=-5 StartY=12 StartZ=0 EndX=-4 EndY=12 EndZ=0
  constraints (40):
    c: Coincident(g0,g1)
    c: Coincident(g1,g2)
    c: Coincident(g2,g3)
    c: Coincident(g3,g0)
    c: Vertical(g0)
    c: Vertical(g2)
    c: Horizontal(g1)
    c: Horizontal(g3)
    c: Coincident(g4,g5)
    c: Coincident(g5,g6)
    c: Coincident(g6,g7)
    c: Coincident(g7,g4)
    c: Vertical(g4)
    c: Vertical(g6)
    c: Horizontal(g5)
    c: Horizontal(g7)
    c: Coincident(g8,g9)
    c: Coincident(g9,g10)
    c: Coincident(g10,g11)
    c: Coincident(g11,g8)
    c: Vertical(g8)
    c: Vertical(g10)
    c: Horizontal(g9)
    c: Horizontal(g11)
    c: Horizontal(g1,g4)
    c: Horizontal(g5,g8)
    c: Coincident(g12,g1)
    c: Coincident(g12,g4)
    c: Coincident(g13,g5)
    c: Coincident(g13,g8)
    c: Equal(g1,g12)
    c: Equal(g12,g5)
    c: Equal(g5,g13)
    c: Equal(g13,g9)
    c: DistanceX(g9,g9) = 1
    c: Horizontal(g2,g4)
    c: Horizontal(g6,g8)
    c: DistanceY(g10,g10) = 4
    c: Distance(g-1,g5) = 12
    c: Distance(g-2,g10) = 3
FEATURE [PartDesign::Pad] Pad092
  BaseFeature = -> Pad091
  Direction = (0,0,1)
  Length = 7.5
  Length2 = 10
  Profile = -> Sketch110
  ReferenceAxis = -> Sketch110 [N_Axis]
  Refine = true
  SideType = 0
  Suppressed = false
  Type = 0
  Type2 = 0
FEATURE [PartDesign::Fillet] Fillet050
  Base = -> Pad092 [Edge929,Edge917,Edge905]
  BaseFeature = -> Pad092
  Radius = 3.9
  Refine = true
  SupportTransform = false
  Suppressed = false
  UseAllEdges = false
FEATURE [PartDesign::Body] Body017  label="Bottom_Part"
  AllowCompound = false
  Group = -> [Sketch099,Pad084,Pad086,Pad085,Sketch100,Sketch101,Pocket039,Mirrored010,Sketch102,Pocket040,Sketch103,Pocket041,Sketch104,Chamfer013,Pocket042,Chamfer012,Fillet049,Sketch105,Pad087,Chamfer014,Chamfer015,Sketch106,Pad088,Sketch107,Pocket043,Sketch108,Pad089,Pad090,Sketch109,Pad091,Sketch110,Pad092,Fillet050]
  Origin = -> Origin031
  Placement = pos=(0,0,-90.8) rot=(0,0,1;0rad)
  Tip = -> Fillet050
FEATURE [PartDesign::Pad] Pad095
  BaseFeature = -> Fillet023
  Direction = (1,0,0)
  Length = 34
  Length2 = -18
  Profile = -> Sketch007
  ReferenceAxis = -> Sketch007 [N_Axis]
  Refine = true
  SideType = 1
  Suppressed = false
  Type = 0
  Type2 = 0
FEATURE [PartDesign::Pad] Pad096
  BaseFeature = -> Pad095
  Direction = (0,-1,2e-16)
  Length = 38.8
  Length2 = -8
  Profile = -> Sketch008
  ReferenceAxis = -> Sketch008 [N_Axis]
  Refine = true
  SideType = 1
  Suppressed = false
  Type = 0
  Type2 = 0
FEATURE [PartDesign::Mirrored] Mirrored012
  BaseFeature = -> Pad096
  MirrorPlane = -> YZ_Plane
  Originals = -> [Pad095]
  Refine = true
  Suppressed = false
  TransformMode = 0
FEATURE [Part::Part2DObjectPython] ShapeString  # Draft 2D object (typed FeaturePython)
  FontFile = /run/current-system/sw/share/fonts/truetype/Orbitron[wght].ttf
  Fuse = false
  Justification = 6
  JustificationReference = 0
  KeepLeftMargin = false
  MakeFace = true
  ObliqueAngle = 0
  Placement = pos=(-44.75,-25,29) rot=(1,0,0;1.5708rad)
  ScaleToSize = true
  Size = 8
  String = sensors.social
  Tracking = 0
FEATURE [PartDesign::Pocket] Pocket045
  BaseFeature = -> Mirrored012
  Direction = (0,1,-2e-16)
  Length = 0.5
  Length2 = 5
  Profile = -> ShapeString
  ReferenceAxis = -> ShapeString [N_Axis]
  Refine = true
  SideType = 0
  Suppressed = false
  Type = 0
  Type2 = 0
FEATURE [Part::FeaturePython] ScrewDie  label="(M22)x5-ScrewDie"  # WARN: FeaturePython — macro-defined, semantics opaque (R4)
  Diameter = 16
  DiameterCustom = 6
  Invert = false
  LeftHanded = false
  Length = 5
  MatchOuter = false
  OffsetAngle = 0
  PitchCustom = 1
  Placement = pos=(0,-8.4e-15,-18.86) rot=(1,0,0;3.14159rad)
  Thread = true
  Type = 0
FEATURE [PartDesign::Chamfer] Chamfer
  Angle = 45
  Base = -> Revolution [Edge16]
  BaseFeature = -> Revolution
  ChamferType = 0
  FlipDirection = false
  Placement = pos=(0,0,0) rot=(1,0,0;1.5708rad)
  Refine = true
  Size = 2.99
  Size2 = 1
  SupportTransform = false
  Suppressed = false
  UseAllEdges = false
FEATURE [PartDesign::Boolean] Boolean
  BaseFeature = -> Chamfer
  Group = -> [ScrewDie]
  Refine = true
  Suppressed = false
  Type = 1
FEATURE [PartDesign::Body] Body001  label="Antena"
  AllowCompound = false
  Group = -> [Sketch009,Revolution,Chamfer,Boolean]
  Origin = -> Origin001
  Placement = pos=(0,0,51.7) rot=(0,0,1;0rad)
  Tip = -> Boolean
FEATURE [Sketcher::SketchObject] Sketch111
  ArcFitTolerance = 1e-06
  AttachmentSupport = -> [Pocket003]
  ExternalTypes = [0]
  FullyConstrained = true
  MakeInternals = false
  MapMode = 5
  Placement = pos=(0,0,2.5) rot=(0,0,1;0rad)
  _ExternalGeoVersion = 1
  sketch-geometry (10):
    g0: LineSegment StartX=-51.5 StartY=-23.4 StartZ=0 EndX=51.5 EndY=-23.4 EndZ=0
    g1: LineSegment StartX=51.5 StartY=23.4 StartZ=0 EndX=-51.5 EndY=23.4 EndZ=0
    g2: LineSegment StartX=-51.5 StartY=-25 StartZ=0 EndX=51.5 EndY=-25 EndZ=0
    g3: LineSegment StartX=51.5 StartY=25 StartZ=0 EndX=-51.5 EndY=25 EndZ=0
    g4: LineSegment StartX=-51.5 StartY=25 StartZ=0 EndX=-51.5 EndY=23.4 EndZ=0
    g5: LineSegment StartX=51.5 StartY=25 StartZ=0 EndX=51.5 EndY=23.4 EndZ=0
    g6: LineSegment StartX=51.5 StartY=-25 StartZ=0 EndX=51.5 EndY=-23.4 EndZ=0
    g7: LineSegment StartX=-51.5 StartY=-23.4 StartZ=0 EndX=-51.5 EndY=-25 EndZ=0
    g8: LineSegment [constr] StartX=-51.5 StartY=23.4 StartZ=0 EndX=-51.5 EndY=-23.4 EndZ=0
    g9: LineSegment [constr] StartX=51.5 StartY=23.4 StartZ=0 EndX=51.5 EndY=-23.4 EndZ=0
  constraints (26):
    c: Horizontal(g0)
    c: Horizontal(g1)
    c: Symmetric(g0,g1,g-1)
    c: DistanceY(g0,g1) = 46.8
    c: Horizontal(g2)
    c: Horizontal(g3)
    c: Symmetric(g2,g3,g-1)
    c: DistanceY(g2,g3) = 50
    c: DistanceX(g3,g3) = 103
    c: Coincident(g4,g3)
    c: Coincident(g4,g1)
    c: Coincident(g5,g3)
    c: Coincident(g5,g1)
    c: Vertical(g5)
    c: Coincident(g6,g2)
    c: Coincident(g6,g0)
    c: Coincident(g7,g0)
    c: Coincident(g7,g2)
    c: Coincident(g8,g1)
    c: Coincident(g8,g0)
    c: Vertical(g8)
    c: Coincident(g9,g1)
    c: Coincident(g9,g0)
    c: Vertical(g9)
    c: Vertical(g4)
    c: Vertical(g6)
FEATURE [PartDesign::Pocket] Pocket046
  BaseFeature = -> Pocket003
  Direction = (0,0,-1)
  Length = 5
  Length2 = 5
  Profile = -> Sketch111
  ReferenceAxis = -> Sketch111 [N_Axis]
  Refine = true
  SideType = 0
  Suppressed = false
  Type = 1
  Type2 = 0
FEATURE [PartDesign::Fillet] Fillet005
  Base = -> Pocket046 [Edge9,Edge20,Edge13,Edge18]
  BaseFeature = -> Pocket046
  Radius = 1.4
  SupportTransform = false
  Suppressed = false
  UseAllEdges = false
FEATURE [Sketcher::SketchObject] Sketch052
  ArcFitTolerance = 1e-06
  AttachmentSupport = -> [Fillet005]
  ExternalTypes = [0]
  FullyConstrained = true
  MakeInternals = false
  MapMode = 5
  Placement = pos=(0,-1.7e-15,-7.5) rot=(1,0,0;3.14159rad)
  _ExternalGeoVersion = 0
  sketch-geometry (13):
    g0: Circle CenterX=-41 CenterY=-5.5 CenterZ=0 NormalX=0 NormalY=0 NormalZ=1 AngleXU=0 Radius=3.25
    g1: LineSegment StartX=35 StartY=12 StartZ=0 EndX=35 EndY=-12 EndZ=0
    g2: LineSegment StartX=35 StartY=-12 StartZ=0 EndX=37 EndY=-12 EndZ=0
    g3: LineSegment StartX=37 StartY=-12 StartZ=0 EndX=37 EndY=12 EndZ=0
    g4: LineSegment StartX=37 StartY=12 StartZ=0 EndX=35 EndY=12 EndZ=0
    g5: LineSegment StartX=38.5 StartY=12 StartZ=0 EndX=38.5 EndY=-12 EndZ=0
    g6: LineSegment StartX=38.5 StartY=-12 StartZ=0 EndX=40.5 EndY=-12 EndZ=0
    g7: LineSegment StartX=40.5 StartY=-12 StartZ=0 EndX=40.5 EndY=12 EndZ=0
    g8: LineSegment StartX=40.5 StartY=12 StartZ=0 EndX=38.5 EndY=12 EndZ=0
    g9: LineSegment StartX=44 StartY=12 StartZ=0 EndX=42 EndY=12 EndZ=0
    g10: LineSegment StartX=42 StartY=12 StartZ=0 EndX=42 EndY=-12 EndZ=0
    g11: LineSegment StartX=42 StartY=-12 StartZ=0 EndX=44 EndY=-12 EndZ=0
    g12: LineSegment StartX=44 StartY=-12 StartZ=0 EndX=44 EndY=12 EndZ=0
  constraints (38):
    c: DistanceX(g0,g-1) = 41
    c: Diameter(g0) = 6.5
    c: Distance(g0,g-1) = 5.5
    c: Coincident(g1,g2)
    c: Coincident(g2,g3)
    c: Coincident(g3,g4)
    c: Coincident(g4,g1)
    c: Vertical(g3)
    c: Horizontal(g2)
    c: Horizontal(g4)
    c: Coincident(g5,g6)
    c: Coincident(g6,g7)
    c: Coincident(g7,g8)
    c: Coincident(g8,g5)
    c: Vertical(g5)
    c: Vertical(g7)
    c: Horizontal(g6)
    c: Horizontal(g8)
    c: Coincident(g9,g10)
    c: Coincident(g10,g11)
    c: Coincident(g11,g12)
    c: Coincident(g12,g9)
    c: Horizontal(g9)
    c: Horizontal(g11)
    c: Vertical(g10)
    c: Vertical(g12)
    c: Equal(g1,g5)
    c: Equal(g1,g10)
    c: Symmetric(g1,g1,g-1)
    c: Horizontal(g3,g5)
    c: Horizontal(g3,g9)
    c: Equal(g4,g8)
    c: Equal(g4,g9)
    c: Distance(g-1,g4) = 12
    c: DistanceX(g4,g4) = 2
    c: Distance(g5,g3) = 1.5
    c: Distance(g10,g7) = 1.5
    c: Distance(g1,g-2) = 35
FEATURE [PartDesign::Fillet] Fillet042
  Base = -> Fillet005 [Edge24,Edge30,Edge42,Edge37,Edge6,Edge18]
  BaseFeature = -> Fillet005
  Radius = 1
  Refine = true
  SupportTransform = false
  Suppressed = false
  UseAllEdges = false
FEATURE [Sketcher::SketchObject] Sketch014
  ArcFitTolerance = 1e-06
  AttachmentSupport = -> [Fillet042]
  ExternalTypes = [0]
  FullyConstrained = true
  MakeInternals = false
  MapMode = 5
  Placement = pos=(49.9,0,0) rot=(0.57735,0.57735,0.57735;2.0944rad)
  _ExternalGeoVersion = 0
  sketch-geometry (6):
    g0: LineSegment StartX=23.4 StartY=5.55 StartZ=0 EndX=23.4 EndY=4.45 EndZ=0
    g1: LineSegment StartX=-23.4 StartY=5.55 StartZ=0 EndX=-23.4 EndY=4.45 EndZ=0
    g2: LineSegment StartX=-23.4 StartY=5.55 StartZ=0 EndX=-22.65 EndY=5.55 EndZ=0
    g3: LineSegment StartX=-22.65 StartY=5.55 StartZ=0 EndX=-23.4 EndY=4.45 EndZ=0
    g4: LineSegment StartX=23.4 StartY=5.55 StartZ=0 EndX=22.65 EndY=5.55 EndZ=0
    g5: LineSegment StartX=22.65 StartY=5.55 StartZ=0 EndX=23.4 EndY=4.45 EndZ=0
  constraints (17):
    c: Vertical(g0)
    c: Vertical(g1)
    c: Equal(g0,g1)
    c: DistanceY(g0,g0) = 1.1
    c: Symmetric(g0,g1,g-2)
    c: DistanceX(g1,g0) = 46.8
    c: Coincident(g1,g2)
    c: Horizontal(g2)
    c: Coincident(g2,g3)
    c: Coincident(g3,g1)
    c: Coincident(g0,g4)
    c: Horizontal(g4)
    c: Coincident(g4,g5)
    c: Coincident(g5,g0)
    c: Distance(g4,g4) = 0.75
    c: Distance(g0,g-1) = 4.45
    c: Equal(g2,g4)
FEATURE [PartDesign::Pocket] Pocket021
  BaseFeature = -> Fillet042
  Direction = (0,0,1)
  Length = 5
  Length2 = 5
  Profile = -> Sketch052
  ReferenceAxis = -> Sketch052 [N_Axis]
  SideType = 0
  Suppressed = false
  Type = 1
  Type2 = 0
FEATURE [PartDesign::Pocket] Pocket
  BaseFeature = -> Pocket021
  Direction = (0,1,-2e-16)
  Length = 41.8
  Length2 = -5
  Profile = -> Sketch013
  ReferenceAxis = -> Sketch013 [N_Axis]
  Refine = true
  SideType = 1
  Suppressed = false
  Type = 0
  Type2 = 0
FEATURE [PartDesign::Pocket] Pocket044
  BaseFeature = -> Pocket
  Direction = (-1,0,0)
  Length = 35
  Length2 = -17
  Profile = -> Sketch014
  ReferenceAxis = -> Sketch014 [N_Axis]
  Refine = true
  SideType = 1
  Suppressed = false
  Type = 0
  Type2 = 0
FEATURE [PartDesign::Mirrored] Mirrored011
  BaseFeature = -> Pocket044
  MirrorPlane = -> YZ_Plane002
  Originals = -> [Pocket044]
  Refine = true
  Suppressed = false
  TransformMode = 0
FEATURE [Sketcher::SketchObject] Sketch112
  ArcFitTolerance = 1e-06
  AttachmentSupport = -> [Pocket045]
  ExternalTypes = [0]
  FullyConstrained = true
  MakeInternals = false
  MapMode = 5
  Placement = pos=(0,-1.94e-14,-44) rot=(1,0,0;3.14159rad)
  _ExternalGeoVersion = 1
  sketch-geometry (10):
    g0: LineSegment StartX=-51.5 StartY=-23.4 StartZ=0 EndX=51.5 EndY=-23.4 EndZ=0
    g1: LineSegment StartX=51.5 StartY=23.4 StartZ=0 EndX=-51.5 EndY=23.4 EndZ=0
    g2: LineSegment StartX=-51.5 StartY=-25 StartZ=0 EndX=51.5 EndY=-25 EndZ=0
    g3: LineSegment StartX=51.5 StartY=25 StartZ=0 EndX=-51.5 EndY=25 EndZ=0
    g4: LineSegment StartX=-51.5 StartY=25 StartZ=0 EndX=-51.5 EndY=23.4 EndZ=0
    g5: LineSegment StartX=51.5 StartY=25 StartZ=0 EndX=51.5 EndY=23.4 EndZ=0
    g6: LineSegment StartX=51.5 StartY=-25 StartZ=0 EndX=51.5 EndY=-23.4 EndZ=0
    g7: LineSegment StartX=-51.5 StartY=-23.4 StartZ=0 EndX=-51.5 EndY=-25 EndZ=0
    g8: LineSegment [constr] StartX=-51.5 StartY=23.4 StartZ=0 EndX=-51.5 EndY=-23.4 EndZ=0
    g9: LineSegment [constr] StartX=51.5 StartY=23.4 StartZ=0 EndX=51.5 EndY=-23.4 EndZ=0
  constraints (26):
    c: Horizontal(g0)
    c: Horizontal(g1)
    c: Symmetric(g0,g1,g-1)
    c: DistanceY(g0,g1) = 46.8
    c: Horizontal(g2)
    c: Horizontal(g3)
    c: Symmetric(g2,g3,g-1)
    c: DistanceY(g2,g3) = 50
    c: DistanceX(g3,g3) = 103
    c: Coincident(g4,g3)
    c: Coincident(g4,g1)
    c: Coincident(g5,g3)
    c: Coincident(g5,g1)
    c: Vertical(g5)
    c: Coincident(g6,g2)
    c: Coincident(g6,g0)
    c: Coincident(g7,g0)
    c: Coincident(g7,g2)
    c: Coincident(g8,g1)
    c: Coincident(g8,g0)
    c: Vertical(g8)
    c: Coincident(g9,g1)
    c: Coincident(g9,g0)
    c: Vertical(g9)
    c: Vertical(g4)
    c: Vertical(g6)
FEATURE [PartDesign::Pad] Pad097
  BaseFeature = -> Pocket045
  Direction = (0,0,-1)
  Length = 10
  Length2 = 10
  Profile = -> Sketch112
  ReferenceAxis = -> Sketch112 [N_Axis]
  Refine = true
  SideType = 0
  Suppressed = false
  Type = 0
  Type2 = 0
FEATURE [PartDesign::Fillet] Fillet051
  Base = -> Pad097 [Edge23,Edge19,Edge16,Edge12]
  BaseFeature = -> Pad097
  Radius = 7
  Refine = true
  SupportTransform = false
  Suppressed = false
  UseAllEdges = false
FEATURE [PartDesign::Body] Body  label="Emotion_Part_Minimal"
  AllowCompound = false
  Group = -> [Sketch,Pad,Fillet,Thickness,Sketch004,Pocket001,Sketch005,Pad004,LinearPattern,Sketch006,Groove,Mirrored001,Sketch007,Sketch008,Fillet023,Pad095,Pad096,Mirrored012,ShapeString,Pocket045,Sketch112,Pad097,Fillet051]
  Origin = -> Origin
  Tip = -> Fillet051
FEATURE [PartDesign::FeatureBase] Clone003
  BaseFeature = -> Body
  Suppressed = false
FEATURE [Sketcher::SketchObject] Sketch002
  ArcFitTolerance = 1e-06
  AttachmentSupport = -> [Clone003]
  ExternalTypes = [0]
  FullyConstrained = true
  MakeInternals = false
  MapMode = 5
  Placement = pos=(0,1.8e-14,41) rot=(1,0,0;3.14159rad)
  _ExternalGeoVersion = 0
  sketch-geometry (1):
    g0: Circle CenterX=0 CenterY=0 CenterZ=0 NormalX=0 NormalY=0 NormalZ=1 AngleXU=0 Radius=12.5
  constraints (2):
    c: Diameter(g0) = 25
    c: Coincident(g0,g-1)
FEATURE [PartDesign::Pad] Pad040
  BaseFeature = -> Clone003
  Direction = (0,0,-1)
  Length = 8
  Length2 = 10
  Profile = -> Sketch002
  ReferenceAxis = -> Sketch002 [N_Axis]
  Refine = true
  SideType = 0
  Suppressed = false
  Type = 0
  Type2 = 0
FEATURE [Sketcher::SketchObject] Sketch003
  ArcFitTolerance = 1e-06
  AttachmentSupport = -> [Pad040]
  ExternalTypes = [0]
  FullyConstrained = true
  MakeInternals = false
  MapMode = 5
  Placement = pos=(-51.5,0,0) rot=(0.57735,-0.57735,-0.57735;2.0944rad)
  _ExternalGeoVersion = 0
  sketch-geometry (2):
    g0: Circle CenterX=0 CenterY=0 CenterZ=0 NormalX=0 NormalY=0 NormalZ=1 AngleXU=0 Radius=11.5
    g1: Circle CenterX=0 CenterY=0 CenterZ=0 NormalX=0 NormalY=0 NormalZ=1 AngleXU=0 Radius=7
  constraints (4):
    c: Diameter(g0) = 23
    c: Coincident(g0,g-1)
    c: Diameter(g1) = 14
    c: Coincident(g1,g0)
FEATURE [PartDesign::Pad] Pad041
  BaseFeature = -> Pad040
  Direction = (-1,1e-16,-1e-16)
  Length = 5.3
  Length2 = 10
  Profile = -> Sketch003 [Edge1]
  ReferenceAxis = -> Sketch003 [N_Axis]
  Refine = true
  SideType = 0
  Suppressed = false
  Type = 0
  Type2 = 0
FEATURE [PartDesign::Pad] Pad042
  BaseFeature = -> Pad041
  Direction = (-1,1e-16,-1e-16)
  Length = 12
  Length2 = 10
  Profile = -> Sketch003 [Edge2]
  ReferenceAxis = -> Sketch003 [N_Axis]
  Refine = true
  SideType = 0
  Suppressed = false
  Type = 0
  Type2 = 0
FEATURE [PartDesign::Fillet] Fillet026
  Base = -> Pad042 [Edge1271]
  BaseFeature = -> Pad042
  Radius = 6.69
  Refine = true
  SupportTransform = false
  Suppressed = false
  UseAllEdges = false
FEATURE [PartDesign::Fillet] Fillet027
  Base = -> Fillet026 [Edge6]
  BaseFeature = -> Fillet026
  Radius = 4.49
  Refine = true
  SupportTransform = false
  Suppressed = false
  UseAllEdges = false
FEATURE [PartDesign::Mirrored] Mirrored
  BaseFeature = -> Fillet027
  MirrorPlane = -> YZ_Plane008
  Originals = -> [Pad041,Pad042,Fillet026,Fillet027]
  Refine = true
  Suppressed = false
  TransformMode = 0
FEATURE [Sketcher::SketchObject] Sketch001
  ArcFitTolerance = 1e-06
  AttachmentSupport = -> [Clone003]
  ExternalTypes = [0]
  FullyConstrained = true
  MakeInternals = false
  MapMode = 5
  Placement = pos=(0,1.94e-14,44) rot=(0,0,1;0rad)
  _ExternalGeoVersion = 0
  sketch-geometry (1):
    g0: GeomPoint X=0 Y=0 Z=0
  constraints (1):
    c: Coincident(g0,g-1)
FEATURE [PartDesign::Fillet] Fillet040
  Base = -> Mirrored [Edge18,Edge68,Edge70,Edge72,Edge74,Edge73,Edge71,Edge67,Edge44,Edge42,Edge46,Edge47,Edge45,Edge43,Edge14,Edge39]
  BaseFeature = -> Mirrored
  Radius = 1
  Refine = true
  SupportTransform = false
  Suppressed = false
  UseAllEdges = false
FEATURE [PartDesign::Fillet] Fillet041
  Base = -> Fillet040 [Edge9,Edge88]
  BaseFeature = -> Fillet040
  Radius = 1
  Refine = true
  SupportTransform = false
  Suppressed = false
  UseAllEdges = false
FEATURE [PartDesign::Hole] Hole
  BaseFeature = -> Fillet041
  BaseProfileType = 7
  CustomThreadClearance = 0
  Depth = 9
  DepthType = 0
  Diameter = 19.542
  DrillForDepth = false
  DrillPoint = 1
  DrillPointAngle = 118
  HoleCutCountersinkAngle = 90
  HoleCutCustomValues = false
  HoleCutDepth = 12.5
  HoleCutDiameter = 25
  HoleCutType = 2
  ModelThread = true
  Profile = -> Sketch001 [Vertex1]
  Refine = true
  Suppressed = false
  Tapered = false
  TaperedAngle = 90
  ThreadClass = 0
  ThreadDepth = 9
  ThreadDepthType = 0
  ThreadDiameter = 22
  ThreadDirection = 0
  ThreadFit = 0
  ThreadSize = 25
  ThreadType = 1
  Threaded = true
  UseCustomThreadClearance = false
FEATURE [PartDesign::Pad] Pad077
  BaseFeature = -> Hole
  Direction = (0,0,-1)
  Length = 8
  Length2 = -7
  Profile = -> Sketch002
  ReferenceAxis = -> Sketch002 [N_Axis]
  Refine = true
  SideType = 1
  Suppressed = false
  Type = 0
  Type2 = 0
FEATURE [PartDesign::Fillet] Fillet047
  Base = -> Pad077 [Edge1347]
  BaseFeature = -> Pad077
  Radius = 3
  Refine = true
  SupportTransform = false
  Suppressed = false
  UseAllEdges = false
FEATURE [PartDesign::Body] Body008  label="Emotion_Part_No_Face"
  AllowCompound = false
  Group = -> [Clone003,Sketch001,Sketch002,Sketch003,Pad040,Pad041,Pad042,Fillet026,Fillet027,Mirrored,Fillet040,Fillet041,Hole,Pad077,Fillet047]
  Origin = -> Origin008
  Tip = -> Fillet047
FEATURE [PartDesign::FeatureBase] Clone004
  BaseFeature = -> Body008
  Suppressed = false
FEATURE [Sketcher::SketchObject] Sketch059  label="Sketch_Deadly"
  ArcFitTolerance = 1e-06
  AttachmentSupport = -> [Clone004]
  ExternalTypes = [0]
  FullyConstrained = true
  MakeInternals = false
  MapMode = 5
  Placement = pos=(0,25,0) rot=(0,0.707107,0.707107;3.14159rad)
  _ExternalGeoVersion = 0
  sketch-geometry (26):
    g0: LineSegment [constr] StartX=0 StartY=18.3137 StartZ=0 EndX=-5.65685 EndY=12.6569 EndZ=0
    g1: LineSegment [constr] StartX=-5.65685 StartY=12.6569 StartZ=0 EndX=0 EndY=7 EndZ=0
    g2: LineSegment [constr] StartX=0 StartY=7 StartZ=0 EndX=5.65685 EndY=12.6569 EndZ=0
    g3: LineSegment [constr] StartX=5.65685 StartY=12.6569 StartZ=0 EndX=0 EndY=18.3137 EndZ=0
    g4: LineSegment StartX=-5.65685 StartY=12.6569 StartZ=0 EndX=-16.9706 EndY=23.9706 EndZ=0
    g5: LineSegment StartX=0 StartY=18.3137 StartZ=0 EndX=-11.3137 EndY=29.6274 EndZ=0
    g6: LineSegment [constr] StartX=-16.9706 StartY=23.9706 StartZ=0 EndX=-11.3137 EndY=29.6274 EndZ=0
    g7: ArcOfCircle CenterX=-14.1421 CenterY=26.799 CenterZ=0 NormalX=0 NormalY=0 NormalZ=1 AngleXU=0 Radius=4 StartAngle=0.785398 EndAngle=3.92699
    g8: LineSegment StartX=0 StartY=18.3137 StartZ=0 EndX=11.3137 EndY=29.6274 EndZ=0
    g9: LineSegment StartX=5.65685 StartY=12.6569 StartZ=0 EndX=16.9706 EndY=23.9706 EndZ=0
    g10: LineSegment [constr] StartX=11.3137 StartY=29.6274 StartZ=0 EndX=16.9706 EndY=23.9706 EndZ=0
    g11: ArcOfCircle CenterX=14.1421 CenterY=26.799 CenterZ=0 NormalX=0 NormalY=0 NormalZ=1 AngleXU=0 Radius=4 StartAngle=5.49779 EndAngle=8.63938
    g12: LineSegment StartX=0 StartY=7 StartZ=0 EndX=11.3137 EndY=-4.31371 EndZ=0
    g13: LineSegment StartX=5.65685 StartY=12.6569 StartZ=0 EndX=16.9706 EndY=1.34315 EndZ=0
    g14: LineSegment [constr] StartX=11.3137 StartY=-4.31371 StartZ=0 EndX=16.9706 EndY=1.34315 EndZ=0
    g15: ArcOfCircle CenterX=14.1421 CenterY=-1.48528 CenterZ=0 NormalX=0 NormalY=0 NormalZ=1 AngleXU=0 Radius=4 StartAngle=3.92699 EndAngle=7.06858
    g16: LineSegment StartX=0 StartY=7 StartZ=0 EndX=-11.3137 EndY=-4.31371 EndZ=0
    g17: LineSegment StartX=-5.65685 StartY=12.6569 StartZ=0 EndX=-16.9706 EndY=1.34315 EndZ=0
    g18: LineSegment [constr] StartX=-16.9706 StartY=1.34315 StartZ=0 EndX=-11.3137 EndY=-4.31371 EndZ=0
    g19: ArcOfCircle CenterX=-14.1421 CenterY=-1.48528 CenterZ=0 NormalX=0 NormalY=0 NormalZ=1 AngleXU=0 Radius=4 StartAngle=2.35619 EndAngle=5.49779
    g20: ArcOfCircle CenterX=0 CenterY=14.7 CenterZ=0 NormalX=0 NormalY=0 NormalZ=1 AngleXU=0 Radius=37.5 StartAngle=3.91338 EndAngle=5.5114
    g21: ArcOfCircle CenterX=0 CenterY=14.7 CenterZ=0 NormalX=0 NormalY=0 NormalZ=1 AngleXU=0 Radius=44.4995 StartAngle=3.91552 EndAngle=5.50926
    g22: LineSegment [constr] StartX=-31.8247 StartY=-16.4028 StartZ=0 EndX=-26.875 EndY=-11.4531 EndZ=0
    g23: LineSegment [constr] StartX=31.8247 StartY=-16.4028 StartZ=0 EndX=26.875 EndY=-11.4531 EndZ=0
    g24: ArcOfCircle CenterX=-29.3499 CenterY=-13.928 CenterZ=0 NormalX=0 NormalY=0 NormalZ=1 AngleXU=0 Radius=3.5 StartAngle=0.785398 EndAngle=3.92699
    g25: ArcOfCircle CenterX=29.3499 CenterY=-13.928 CenterZ=0 NormalX=0 NormalY=0 NormalZ=1 AngleXU=0 Radius=3.5 StartAngle=5.49779 EndAngle=8.63938
  constraints (76):
    c: PointOnObject(g0,g-2)
    c: Coincident(g1,g0)
    c: PointOnObject(g1,g-2)
    c: PointOnObject(g2,g-2)
    c: Coincident(g3,g2)
    c: Coincident(g3,g0)
    c: Perpendicular(g1,g0)
    c: Perpendicular(g2,g1)
    c: Equal(g0,g3)
    c: Equal(g1,g0)
    c: Equal(g2,g0)
    c: Distance(g0,g0) = 8
    c: Coincident(g4,g0)
    c: Coincident(g5,g0)
    c: Coincident(g6,g4)
    c: Coincident(g6,g5)
    c: Parallel(g5,g3)
    c: Parallel(g6,g0)
    c: Coincident(g7,g5)
    c: Coincident(g7,g4)
    c: PointOnObject(g7,g6)
    c: Parallel(g4,g5)
    c: Distance(g5,g5) = 16
    c: Coincident(g8,g0)
    c: Coincident(g9,g2)
    c: Parallel(g8,g9)
    c: Parallel(g8,g0)
    c: Coincident(g10,g8)
    c: Coincident(g10,g9)
    c: Parallel(g3,g10)
    c: Equal(g5,g8)
    c: Coincident(g11,g8)
    c: Coincident(g11,g9)
    c: PointOnObject(g11,g10)
    c: Coincident(g12,g1)
    c: Coincident(g13,g2)
    c: Coincident(g14,g12)
    c: Coincident(g14,g13)
    c: Parallel(g2,g14)
    c: Parallel(g12,g13)
    c: Parallel(g13,g3)
    c: Equal(g13,g5)
    c: Coincident(g15,g13)
    c: Coincident(g15,g12)
    c: PointOnObject(g15,g14)
    c: Coincident(g16,g2)
    c: Coincident(g17,g0)
    c: Coincident(g18,g17)
    c: Coincident(g18,g16)
    c: Parallel(g18,g1)
    c: Parallel(g17,g16)
    c: Parallel(g17,g0)
    c: Equal(g5,g17)
    c: Coincident(g19,g17)
    c: Coincident(g19,g16)
    c: PointOnObject(g19,g18)
    c: Coincident(g21,g20)
    c: Coincident(g22,g21)
    c: Coincident(g22,g20)
    c: Coincident(g23,g21)
    c: Coincident(g23,g20)
    c: Coincident(g24,g21)
    c: Coincident(g24,g20)
    c: Coincident(g25,g20)
    c: Coincident(g25,g21)
    c: PointOnObject(g25,g23)
    c: PointOnObject(g24,g22)
    c: Parallel(g22,g0)
    c: Parallel(g23,g3)
    c: Radius(g25) = 3.5
    c: Radius(g20) = 37.5
    c: DistanceY(g-1,g20) = 14.7
    c: PointOnObject(g20,g-2)
    c: Horizontal(g20,g20)
    c: DistanceX(g20,g20) = 53.75
    c: DistanceY(g-1,g1) = 7
FEATURE [PartDesign::FeatureBase] Clone005
  BaseFeature = -> Body008
  Suppressed = false
FEATURE [Sketcher::SketchObject] Sketch060  label="Sketch_Smile"
  ArcFitTolerance = 1e-06
  AttachmentSupport = -> [Clone005]
  ExternalTypes = [0]
  FullyConstrained = true
  MakeInternals = false
  MapMode = 5
  Placement = pos=(0,25,0) rot=(0,0.707107,0.707107;3.14159rad)
  _ExternalGeoVersion = 0
  sketch-geometry (8):
    g0: ArcOfCircle CenterX=-3.6e-15 CenterY=15 CenterZ=0 NormalX=0 NormalY=0 NormalZ=1 AngleXU=0 Radius=37.5 StartAngle=3.92699 EndAngle=5.49779
    g1: ArcOfCircle CenterX=-3.6e-15 CenterY=15 CenterZ=0 NormalX=0 NormalY=0 NormalZ=1 AngleXU=0 Radius=44.5 StartAngle=3.92699 EndAngle=5.49779
    g2: ArcOfCircle CenterX=-28.9914 CenterY=-13.9914 CenterZ=0 NormalX=0 NormalY=0 NormalZ=1 AngleXU=0 Radius=3.5 StartAngle=0.785398 EndAngle=3.92699
    g3: ArcOfCircle CenterX=28.9914 CenterY=-13.9914 CenterZ=0 NormalX=0 NormalY=0 NormalZ=1 AngleXU=0 Radius=3.5 StartAngle=5.49779 EndAngle=8.63938
    g4: LineSegment [constr] StartX=-31.4663 StartY=-16.4663 StartZ=0 EndX=-3.6e-15 EndY=15 EndZ=0
    g5: LineSegment [constr] StartX=31.4663 StartY=-16.4663 StartZ=0 EndX=-3.6e-15 EndY=15 EndZ=0
    g6: Circle CenterX=0 CenterY=8.5 CenterZ=0 NormalX=0 NormalY=0 NormalZ=1 AngleXU=0 Radius=13
    g7: Circle CenterX=0 CenterY=8.5 CenterZ=0 NormalX=0 NormalY=0 NormalZ=1 AngleXU=0 Radius=19
  constraints (24):
    c: Coincident(g1,g0)
    c: Coincident(g2,g1)
    c: Coincident(g2,g0)
    c: Coincident(g3,g0)
    c: Coincident(g3,g1)
    c: Radius(g3) = 3.5
    c: Radius(g0) = 37.5
    c: DistanceY(g-1,g0) = 15
    c: PointOnObject(g0,g-2)
    c: Horizontal(g0,g0)
    c: Coincident(g4,g1)
    c: Coincident(g4,g0)
    c: PointOnObject(g2,g4)
    c: PointOnObject(g0,g4)
    c: Coincident(g5,g1)
    c: Coincident(g5,g0)
    c: PointOnObject(g3,g5)
    c: PointOnObject(g0,g5)
    c: Angle(g4,g5) = 1.5708
    c: Coincident(g7,g6)
    c: Diameter(g6) = 26
    c: Diameter(g7) = 38
    c: PointOnObject(g6,g-2)
    c: DistanceY(g-1,g6) = 8.5
FEATURE [PartDesign::FeatureBase] Clone006
  BaseFeature = -> Body008
  Suppressed = false
FEATURE [PartDesign::Pocket] Pocket029
  BaseFeature = -> Clone004
  Direction = (0,-1,2e-16)
  Length = 2
  Length2 = 5
  Profile = -> Sketch059
  ReferenceAxis = -> Sketch059 [N_Axis]
  Refine = true
  SideType = 0
  Suppressed = false
  Type = 0
  Type2 = 0
FEATURE [PartDesign::Pocket] Pocket030
  BaseFeature = -> Clone005
  Direction = (0,-1,2e-16)
  Length = 2
  Length2 = 5
  Profile = -> Sketch060
  ReferenceAxis = -> Sketch060 [N_Axis]
  Refine = true
  SideType = 0
  Suppressed = false
  Type = 0
  Type2 = 0
FEATURE [Sketcher::SketchObject] Sketch061  label="Sketch_Enjoy"
  ArcFitTolerance = 1e-06
  AttachmentSupport = -> [Clone006]
  ExternalTypes = [0]
  FullyConstrained = true
  MakeInternals = false
  MapMode = 5
  Placement = pos=(0,25,0) rot=(0,0.707107,0.707107;3.14159rad)
  _ExternalGeoVersion = 0
  sketch-geometry (27):
    g0: ArcOfCircle CenterX=3.6e-15 CenterY=15 CenterZ=0 NormalX=0 NormalY=0 NormalZ=1 AngleXU=0 Radius=37.5 StartAngle=3.92699 EndAngle=5.49779
    g1: ArcOfCircle CenterX=3.6e-15 CenterY=15 CenterZ=0 NormalX=0 NormalY=0 NormalZ=1 AngleXU=0 Radius=44.5 StartAngle=3.92699 EndAngle=5.49779
    g2: ArcOfCircle CenterX=-28.9914 CenterY=-13.9914 CenterZ=0 NormalX=0 NormalY=0 NormalZ=1 AngleXU=0 Radius=3.5 StartAngle=0.785398 EndAngle=3.92699
    g3: ArcOfCircle CenterX=28.9914 CenterY=-13.9914 CenterZ=0 NormalX=0 NormalY=0 NormalZ=1 AngleXU=0 Radius=3.5 StartAngle=5.49779 EndAngle=8.63938
    g4: LineSegment [constr] StartX=-31.4662 StartY=-16.4663 StartZ=0 EndX=3.6e-15 EndY=15 EndZ=0
    g5: LineSegment [constr] StartX=31.4662 StartY=-16.4663 StartZ=0 EndX=3.6e-15 EndY=15 EndZ=0
    g6: ArcOfCircle CenterX=0 CenterY=3.6e-15 CenterZ=0 NormalX=0 NormalY=0 NormalZ=1 AngleXU=0 Radius=23.25 StartAngle=1.13925 EndAngle=1.47819
    g7: ArcOfCircle CenterX=0 CenterY=3.6e-15 CenterZ=0 NormalX=0 NormalY=0 NormalZ=1 AngleXU=0 Radius=23.25 StartAngle=2.1935 EndAngle=2.44346
    g8: ArcOfCircle CenterX=0 CenterY=3.6e-15 CenterZ=0 NormalX=0 NormalY=0 NormalZ=1 AngleXU=0 Radius=23.25 StartAngle=1.6634 EndAngle=2.00235
    g9: ArcOfCircle CenterX=0 CenterY=3.6e-15 CenterZ=0 NormalX=0 NormalY=0 NormalZ=1 AngleXU=0 Radius=23.25 StartAngle=0.698132 EndAngle=0.948097
    g10: ArcOfCircle CenterX=0 CenterY=3.6e-15 CenterZ=0 NormalX=0 NormalY=0 NormalZ=1 AngleXU=0 Radius=15.45 StartAngle=0.698132 EndAngle=2.44346
    g11: LineSegment [constr] StartX=-17.8105 StartY=14.9448 StartZ=0 EndX=0 EndY=3.6e-15 EndZ=0
    g12: LineSegment [constr] StartX=17.8105 StartY=14.9448 StartZ=0 EndX=0 EndY=3.6e-15 EndZ=0
    g13: ArcOfCircle CenterX=-14.823 CenterY=12.4379 CenterZ=0 NormalX=0 NormalY=0 NormalZ=1 AngleXU=0 Radius=3.9 StartAngle=2.44346 EndAngle=5.58505
    g14: ArcOfCircle CenterX=14.823 CenterY=12.4379 CenterZ=0 NormalX=0 NormalY=0 NormalZ=1 AngleXU=0 Radius=3.9 StartAngle=3.83972 EndAngle=6.98132
    g15: LineSegment StartX=-2.15 StartY=23.1504 StartZ=0 EndX=-2.15 EndY=28.7504 EndZ=0
    g16: LineSegment StartX=2.15 StartY=23.1504 StartZ=0 EndX=2.15 EndY=28.7504 EndZ=0
    g17: LineSegment StartX=9.725 StartY=21.1184 StartZ=0 EndX=13.2295 EndY=24.6847 EndZ=0
    g18: LineSegment StartX=13.5601 StartY=18.8861 StartZ=0 EndX=16.2965 EndY=21.6707 EndZ=0
    g19: LineSegment StartX=-9.725 StartY=21.1184 StartZ=0 EndX=-13.2295 EndY=24.6847 EndZ=0
    g20: LineSegment StartX=-13.5601 StartY=18.8861 StartZ=0 EndX=-16.2965 EndY=21.6707 EndZ=0
    g21: ArcOfCircle CenterX=-14.763 CenterY=23.1777 CenterZ=0 NormalX=0 NormalY=0 NormalZ=1 AngleXU=0 Radius=2.15 StartAngle=0.776672 EndAngle=3.91826
    g22: ArcOfCircle CenterX=6.7e-15 CenterY=28.7504 CenterZ=0 NormalX=0 NormalY=0 NormalZ=1 AngleXU=0 Radius=2.15 StartAngle=0 EndAngle=3.14159
    g23: ArcOfCircle CenterX=14.763 CenterY=23.1777 CenterZ=0 NormalX=0 NormalY=0 NormalZ=1 AngleXU=0 Radius=2.15 StartAngle=5.50651 EndAngle=8.64811
    g24: LineSegment [constr] StartX=-16.2965 StartY=21.6707 StartZ=0 EndX=-13.2295 EndY=24.6847 EndZ=0
    g25: LineSegment [constr] StartX=16.2965 StartY=21.6707 StartZ=0 EndX=13.2295 EndY=24.6847 EndZ=0
    g26: LineSegment [constr] StartX=-2.15 StartY=28.7504 StartZ=0 EndX=2.15 EndY=28.7504 EndZ=0
  constraints (82):
    c: Coincident(g1,g0)
    c: Coincident(g2,g1)
    c: Coincident(g2,g0)
    c: Coincident(g3,g0)
    c: Coincident(g3,g1)
    c: Radius(g3) = 3.5
    c: Radius(g0) = 37.5
    c: DistanceY(g-1,g0) = 15
    c: PointOnObject(g0,g-2)
    c: Horizontal(g0,g0)
    c: Coincident(g4,g1)
    c: Coincident(g4,g0)
    c: PointOnObject(g2,g4)
    c: PointOnObject(g0,g4)
    c: Coincident(g5,g1)
    c: Coincident(g5,g0)
    c: PointOnObject(g3,g5)
    c: PointOnObject(g0,g5)
    c: Angle(g4,g5) = 1.5708
    c: Radius(g9) = 23.25
    c: Coincident(g6,g7)
    c: Coincident(g6,g8)
    c: Coincident(g6,g9)
    c: Coincident(g10,g6)
    c: Equal(g7,g9)
    c: Equal(g8,g9)
    c: Equal(g6,g9)
    c: Radius(g10) = 15.45
    c: Coincident(g11,g7)
    c: Coincident(g11,g6)
    c: Coincident(g12,g9)
    c: Coincident(g12,g11)
    c: PointOnObject(g10,g12)
    c: PointOnObject(g10,g11)
    c: Coincident(g13,g7)
    c: Coincident(g13,g10)
    c: PointOnObject(g13,g11)
    c: Coincident(g14,g9)
    c: Coincident(g14,g10)
    c: PointOnObject(g14,g12)
    c: Angle(g12,g11) = 1.74533
    c: Coincident(g15,g8)
    c: Vertical(g15)
    c: Coincident(g16,g6)
    c: Vertical(g16)
    c: Coincident(g17,g6)
    c: Coincident(g18,g9)
    c: Coincident(g19,g8)
    c: Coincident(g20,g7)
    c: Parallel(g20,g19)
    c: Parallel(g17,g18)
    c: Coincident(g21,g20)
    c: Coincident(g21,g19)
    c: Coincident(g22,g15)
    c: Coincident(g22,g16)
    c: Coincident(g23,g17)
    c: Coincident(g23,g18)
    c: Coincident(g24,g20)
    c: Coincident(g24,g19)
    c: Coincident(g25,g18)
    c: Coincident(g25,g17)
    c: Coincident(g26,g15)
    c: Coincident(g26,g16)
    c: Equal(g26,g25)
    c: Equal(g26,g24)
    c: DistanceX(g26,g26) = 4.3
    c: PointOnObject(g21,g24)
    c: PointOnObject(g22,g26)
    c: PointOnObject(g23,g25)
    c: Angle(g17,g19) = 1.55334
    c: Distance(g19,g19) = 5
    c: Equal(g17,g19)
    c: DistanceY(g16,g16) = 5.6
    c: DistanceX(g8,g6) = 19.45
    c: Coincident(g6,g-1)
    c: Equal(g16,g15)
    c: Horizontal(g8,g6)
    c: Horizontal(g6,g8)
    c: Perpendicular(g17,g25)
    c: Perpendicular(g19,g24)
    c: Horizontal(g17,g19)
    c: Horizontal(g9,g7)
FEATURE [PartDesign::Pocket] Pocket031
  BaseFeature = -> Clone006
  Direction = (0,-1,2e-16)
  Length = 2
  Length2 = 5
  Profile = -> Sketch061
  ReferenceAxis = -> Sketch061 [N_Axis]
  Refine = true
  SideType = 0
  Suppressed = false
  Type = 0
  Type2 = 0
FEATURE [PartDesign::Fillet] Fillet037
  Base = -> Pocket030 [Face429,Face430]
  BaseFeature = -> Pocket030
  Radius = 0.5
  Refine = true
  SupportTransform = false
  Suppressed = false
  UseAllEdges = false
FEATURE [PartDesign::Fillet] Fillet038
  Base = -> Fillet037 [Edge1244,Edge21,Edge6,Edge19,Edge3,Edge20]
  BaseFeature = -> Fillet037
  Radius = 1.49
  Refine = true
  SupportTransform = false
  Suppressed = false
  UseAllEdges = false
FEATURE [PartDesign::Body] Body010  label="Emotion_Part_Smile"
  AllowCompound = false
  Group = -> [Clone005,Sketch060,Pocket030,Fillet037,Fillet038]
  Origin = -> Origin010
  Tip = -> Fillet038
FEATURE [PartDesign::Fillet] Fillet043
  Base = -> Pocket029 [Face440,Face441]
  BaseFeature = -> Pocket029
  Radius = 0.5
  Refine = true
  SupportTransform = false
  Suppressed = false
  UseAllEdges = false
FEATURE [PartDesign::Fillet] Fillet044
  Base = -> Fillet043 [Edge6,Edge3,Edge19,Edge20,Edge25,Edge24,Edge26,Edge27,Edge28,Edge29,Edge30,Edge32,Edge21,Edge23,Edge22,Edge31]
  BaseFeature = -> Fillet043
  Radius = 1.45
  Refine = true
  SupportTransform = false
  Suppressed = false
  UseAllEdges = false
FEATURE [PartDesign::Body] Body009  label="Emotion_Part_Deadly"
  AllowCompound = false
  Group = -> [Clone004,Sketch059,Pocket029,Fillet043,Fillet044]
  Origin = -> Origin009
  Tip = -> Fillet044
FEATURE [PartDesign::Fillet] Fillet045
  Base = -> Pocket031 [Face444,Face445]
  BaseFeature = -> Pocket031
  Radius = 0.5
  Refine = true
  SupportTransform = false
  Suppressed = false
  UseAllEdges = false
FEATURE [PartDesign::Fillet] Fillet046
  Base = -> Fillet045 [Edge36,Edge6,Edge23,Edge27,Edge30,Edge26,Edge22]
  BaseFeature = -> Fillet045
  Radius = 1.45
  Refine = true
  SupportTransform = false
  Suppressed = false
  UseAllEdges = false
FEATURE [PartDesign::Body] Body011  label="Emotion_Part_Enjoy"
  AllowCompound = false
  Group = -> [Clone006,Sketch061,Pocket031,Fillet045,Fillet046]
  Origin = -> Origin011
  Tip = -> Fillet046
FEATURE [PartDesign::Fillet] Fillet052
  Base = -> Mirrored011 [Edge144,Edge147,Edge151,Edge149]
  BaseFeature = -> Mirrored011
  Radius = 1.6
  Refine = true
  SupportTransform = false
  Suppressed = false
  UseAllEdges = false
FEATURE [PartDesign::Body] Body002  label="Central_Part"
  AllowCompound = false
  Group = -> [Sketch010,Pad005,Fillet004,Thickness001,Sketch011,Pocket002,Sketch012,Pocket003,Pocket046,Sketch013,Sketch014,Fillet005,Fillet042,Sketch052,Pocket021,Pocket,Pocket044,Mirrored011,Sketch111,Fillet052]
  Origin = -> Origin002
  Placement = pos=(0,0,-46.5) rot=(0,0,1;0rad)
  Tip = -> Fillet052
